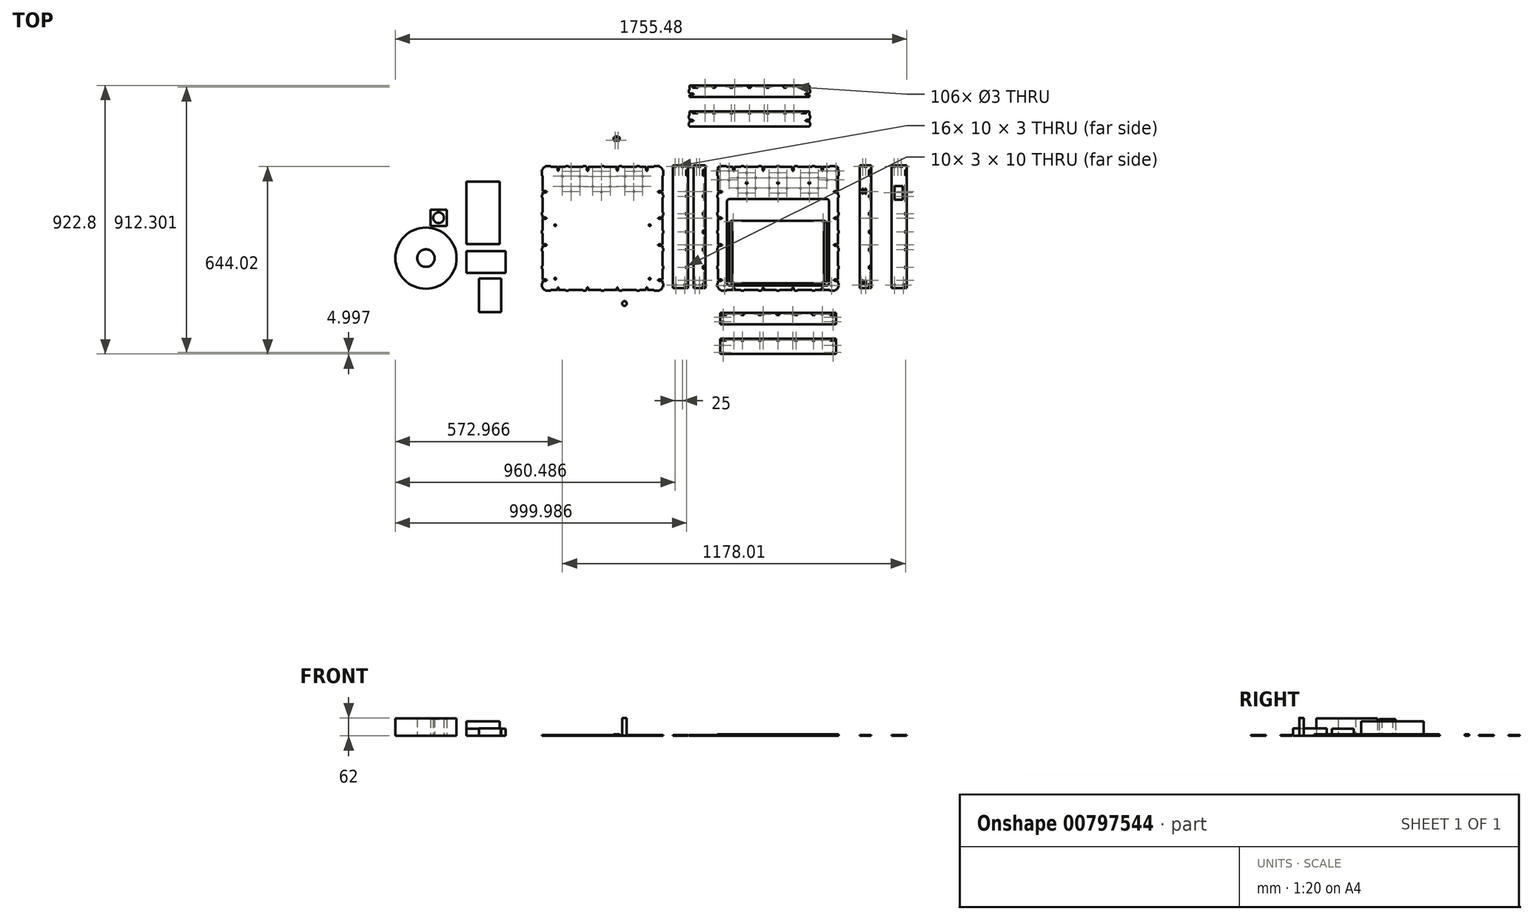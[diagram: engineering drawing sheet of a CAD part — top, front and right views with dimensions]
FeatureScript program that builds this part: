
annotation { "Feature Type Name" : "Feature", "Feature Type Description" : "" }
export const myFeature = defineFeature(function(context is Context, id is Id, definition is map)
    precondition{}
    {
        {
            var Q0;
            Q0=qCreatedBy(makeId("Top.planeOp"),FACE);
            var sketch = newSketch(context, id + "F0", { "sketchPlane" : qUnion([Q0])});
            skCircle(sketch, "E0", {"center": v(-429.2, -257.83) * mm, "radius": 8 * mm});
            skSolve(sketch);
        }
        {
            var Q0;
            Q0=makeQuery(id+"F0.imprint","IMPRINT",FACE,{"disambiguationData":[TD([[makeQuery(id+"F0.imprint","IMPRINT",EDGE,{"derivedFrom":sQuery(id+"F0.wireOp",EDGE,"E0")}),1.0]])]});
            extrude(context, id + "F1", {"entities" : qUnion([Q0]), "depth" : 62 * mm, "offsetDistance" : 25 * mm});
        }
        {
            var Q0;
            Q0=qCreatedBy(makeId("Top.planeOp"),FACE);
            var sketch = newSketch(context, id + "F2", { "sketchPlane" : qUnion([Q0])});
            skLineSegment(sketch, "E1", {"start": v(147.3, -211.25) * mm, "end": v(103, -211.25) * mm});
            skLineSegment(sketch, "E2", {"start": v(147.3, -208.35) * mm, "end": v(147.3, -211.25) * mm});
            skLineSegment(sketch, "E3", {"start": v(147.3, -208.35) * mm, "end": v(145.8, -208.35) * mm});
            skLineSegment(sketch, "E4", {"start": v(145.8, -205.75) * mm, "end": v(145.8, -208.35) * mm});
            skLineSegment(sketch, "E5", {"start": v(147.3, -205.75) * mm, "end": v(145.8, -205.75) * mm});
            skLineSegment(sketch, "E6", {"start": v(147.3, -202.75) * mm, "end": v(147.3, -205.75) * mm});
            skLineSegment(sketch, "E7", {"start": v(150.7, -202.75) * mm, "end": v(147.3, -202.75) * mm});
            skLineSegment(sketch, "E8", {"start": v(150.7, -205.75) * mm, "end": v(150.7, -202.75) * mm});
            skLineSegment(sketch, "E9", {"start": v(152.2, -205.75) * mm, "end": v(150.7, -205.75) * mm});
            skLineSegment(sketch, "E10", {"start": v(152.2, -208.35) * mm, "end": v(152.2, -205.75) * mm});
            skLineSegment(sketch, "E11", {"start": v(152.2, -208.35) * mm, "end": v(150.7, -208.35) * mm});
            skLineSegment(sketch, "E12", {"start": v(150.7, -211.25) * mm, "end": v(150.7, -208.35) * mm});
            skLineSegment(sketch, "E13", {"start": v(155, -211.25) * mm, "end": v(150.7, -211.25) * mm});
            skLineSegment(sketch, "E14", {"start": v(155, -214.25) * mm, "end": v(155, -211.25) * mm});
            skLineSegment(sketch, "E15", {"start": v(165, -214.25) * mm, "end": v(155, -214.25) * mm});
            skLineSegment(sketch, "E16", {"start": v(165, -211.25) * mm, "end": v(165, -214.25) * mm});
            skLineSegment(sketch, "E17", {"start": v(215, -211.25) * mm, "end": v(165, -211.25) * mm});
            skLineSegment(sketch, "E18", {"start": v(215, -214.25) * mm, "end": v(215, -211.25) * mm});
            skLineSegment(sketch, "E19", {"start": v(225, -214.25) * mm, "end": v(215, -214.25) * mm});
            skLineSegment(sketch, "E20", {"start": v(225, -211.25) * mm, "end": v(225, -214.25) * mm});
            skLineSegment(sketch, "E21", {"start": v(248.3, -211.25) * mm, "end": v(225, -211.25) * mm});
            skLineSegment(sketch, "E22", {"start": v(248.3, -208.35) * mm, "end": v(248.3, -211.25) * mm});
            skLineSegment(sketch, "E23", {"start": v(246.8, -208.35) * mm, "end": v(248.3, -208.35) * mm});
            skLineSegment(sketch, "E24", {"start": v(246.8, -205.75) * mm, "end": v(246.8, -208.35) * mm});
            skLineSegment(sketch, "E25", {"start": v(248.3, -205.75) * mm, "end": v(246.8, -205.75) * mm});
            skLineSegment(sketch, "E26", {"start": v(248.3, -202.75) * mm, "end": v(248.3, -205.75) * mm});
            skLineSegment(sketch, "E27", {"start": v(251.7, -202.75) * mm, "end": v(248.3, -202.75) * mm});
            skLineSegment(sketch, "E28", {"start": v(251.7, -205.75) * mm, "end": v(251.7, -202.75) * mm});
            skLineSegment(sketch, "E29", {"start": v(253.2, -205.75) * mm, "end": v(251.7, -205.75) * mm});
            skLineSegment(sketch, "E30", {"start": v(253.2, -208.35) * mm, "end": v(253.2, -205.75) * mm});
            skLineSegment(sketch, "E31", {"start": v(251.7, -208.35) * mm, "end": v(253.2, -208.35) * mm});
            skLineSegment(sketch, "E32", {"start": v(251.7, -211.25) * mm, "end": v(251.7, -208.35) * mm});
            skLineSegment(sketch, "E33", {"start": v(275, -211.25) * mm, "end": v(251.7, -211.25) * mm});
            skLineSegment(sketch, "E34", {"start": v(275, -214.25) * mm, "end": v(275, -211.25) * mm});
            skLineSegment(sketch, "E35", {"start": v(293.5, -214.25) * mm, "end": v(275, -214.25) * mm});
            skLineSegment(sketch, "E36", {"start": v(293.5, -211.25) * mm, "end": v(293.5, -214.25) * mm});
            skArc(sketch, "E37", {"start": v(303.5, -201.25) * mm, "mid": v(300.57, -208.32) * mm, "end": v(293.5, -211.25) * mm});
            skLineSegment(sketch, "E38", {"start": v(306.5, -201.25) * mm, "end": v(303.5, -201.25) * mm});
            skLineSegment(sketch, "E39", {"start": v(306.5, -188.25) * mm, "end": v(306.5, -201.25) * mm});
            skLineSegment(sketch, "E40", {"start": v(303.5, -188.25) * mm, "end": v(306.5, -188.25) * mm});
            skLineSegment(sketch, "E41", {"start": v(303.5, -179.45) * mm, "end": v(303.5, -188.25) * mm});
            skLineSegment(sketch, "E42", {"start": v(297.1, -179.45) * mm, "end": v(303.5, -179.45) * mm});
            skLineSegment(sketch, "E43", {"start": v(297.1, -180.95) * mm, "end": v(297.1, -179.45) * mm});
            skLineSegment(sketch, "E44", {"start": v(294.5, -180.95) * mm, "end": v(297.1, -180.95) * mm});
            skLineSegment(sketch, "E45", {"start": v(294.5, -179.45) * mm, "end": v(294.5, -180.95) * mm});
            skLineSegment(sketch, "E46", {"start": v(289.5, -179.45) * mm, "end": v(294.5, -179.45) * mm});
            skLineSegment(sketch, "E47", {"start": v(289.5, -176.05) * mm, "end": v(289.5, -179.45) * mm});
            skLineSegment(sketch, "E48", {"start": v(294.5, -176.05) * mm, "end": v(289.5, -176.05) * mm});
            skLineSegment(sketch, "E49", {"start": v(294.5, -174.55) * mm, "end": v(294.5, -176.05) * mm});
            skLineSegment(sketch, "E50", {"start": v(297.1, -174.55) * mm, "end": v(294.5, -174.55) * mm});
            skLineSegment(sketch, "E51", {"start": v(297.1, -176.05) * mm, "end": v(297.1, -174.55) * mm});
            skLineSegment(sketch, "E52", {"start": v(303.5, -176.05) * mm, "end": v(297.1, -176.05) * mm});
            skLineSegment(sketch, "E53", {"start": v(303.5, -138.25) * mm, "end": v(303.5, -176.05) * mm});
            skLineSegment(sketch, "E54", {"start": v(306.5, -138.25) * mm, "end": v(303.5, -138.25) * mm});
            skLineSegment(sketch, "E55", {"start": v(306.5, -128.25) * mm, "end": v(306.5, -138.25) * mm});
            skLineSegment(sketch, "E56", {"start": v(303.5, -128.25) * mm, "end": v(306.5, -128.25) * mm});
            skLineSegment(sketch, "E57", {"start": v(303.5, -78.25) * mm, "end": v(303.5, -128.25) * mm});
            skLineSegment(sketch, "E58", {"start": v(306.5, -78.25) * mm, "end": v(303.5, -78.25) * mm});
            skLineSegment(sketch, "E59", {"start": v(306.5, -68.25) * mm, "end": v(306.5, -78.25) * mm});
            skLineSegment(sketch, "E60", {"start": v(303.5, -68.25) * mm, "end": v(306.5, -68.25) * mm});
            skLineSegment(sketch, "E61", {"start": v(303.5, -58.45) * mm, "end": v(303.5, -68.25) * mm});
            skLineSegment(sketch, "E62", {"start": v(297.1, -58.45) * mm, "end": v(303.5, -58.45) * mm});
            skLineSegment(sketch, "E63", {"start": v(297.1, -59.95) * mm, "end": v(297.1, -58.45) * mm});
            skLineSegment(sketch, "E64", {"start": v(294.5, -59.95) * mm, "end": v(297.1, -59.95) * mm});
            skLineSegment(sketch, "E65", {"start": v(294.5, -58.45) * mm, "end": v(294.5, -59.95) * mm});
            skLineSegment(sketch, "E66", {"start": v(289.5, -58.45) * mm, "end": v(294.5, -58.45) * mm});
            skLineSegment(sketch, "E67", {"start": v(289.5, -55.05) * mm, "end": v(289.5, -58.45) * mm});
            skLineSegment(sketch, "E68", {"start": v(294.5, -55.05) * mm, "end": v(289.5, -55.05) * mm});
            skLineSegment(sketch, "E69", {"start": v(294.5, -53.55) * mm, "end": v(294.5, -55.05) * mm});
            skLineSegment(sketch, "E70", {"start": v(297.1, -53.55) * mm, "end": v(294.5, -53.55) * mm});
            skLineSegment(sketch, "E71", {"start": v(297.1, -55.05) * mm, "end": v(297.1, -53.55) * mm});
            skLineSegment(sketch, "E72", {"start": v(303.5, -55.05) * mm, "end": v(297.1, -55.05) * mm});
            skLineSegment(sketch, "E73", {"start": v(303.5, -16.25) * mm, "end": v(303.5, -55.05) * mm});
            skLineSegment(sketch, "E74", {"start": v(306.5, -16.25) * mm, "end": v(303.5, -16.25) * mm});
            skLineSegment(sketch, "E75", {"start": v(306.5, -6.25) * mm, "end": v(306.5, -16.25) * mm});
            skLineSegment(sketch, "E76", {"start": v(303.5, -6.25) * mm, "end": v(306.5, -6.25) * mm});
            skLineSegment(sketch, "E77", {"start": v(303.5, 33.55) * mm, "end": v(303.5, -6.25) * mm});
            skLineSegment(sketch, "E78", {"start": v(297.1, 33.55) * mm, "end": v(303.5, 33.55) * mm});
            skLineSegment(sketch, "E79", {"start": v(297.1, 33.55) * mm, "end": v(297.1, 32.05) * mm});
            skLineSegment(sketch, "E80", {"start": v(294.5, 32.05) * mm, "end": v(297.1, 32.05) * mm});
            skLineSegment(sketch, "E81", {"start": v(294.5, 33.55) * mm, "end": v(294.5, 32.05) * mm});
            skLineSegment(sketch, "E82", {"start": v(289.5, 33.55) * mm, "end": v(294.5, 33.55) * mm});
            skLineSegment(sketch, "E83", {"start": v(289.5, 36.95) * mm, "end": v(289.5, 33.55) * mm});
            skLineSegment(sketch, "E84", {"start": v(294.5, 36.95) * mm, "end": v(289.5, 36.95) * mm});
            skLineSegment(sketch, "E85", {"start": v(294.5, 38.45) * mm, "end": v(294.5, 36.95) * mm});
            skLineSegment(sketch, "E86", {"start": v(297.1, 38.45) * mm, "end": v(294.5, 38.45) * mm});
            skLineSegment(sketch, "E87", {"start": v(297.1, 38.45) * mm, "end": v(297.1, 36.95) * mm});
            skLineSegment(sketch, "E88", {"start": v(303.5, 36.95) * mm, "end": v(297.1, 36.95) * mm});
            skLineSegment(sketch, "E89", {"start": v(303.5, 45.75) * mm, "end": v(303.5, 36.95) * mm});
            skLineSegment(sketch, "E90", {"start": v(306.5, 45.75) * mm, "end": v(303.5, 45.75) * mm});
            skLineSegment(sketch, "E91", {"start": v(306.5, 55.75) * mm, "end": v(306.5, 45.75) * mm});
            skLineSegment(sketch, "E92", {"start": v(303.5, 55.75) * mm, "end": v(306.5, 55.75) * mm});
            skLineSegment(sketch, "E93", {"start": v(303.5, 105.75) * mm, "end": v(303.5, 55.75) * mm});
            skLineSegment(sketch, "E94", {"start": v(306.5, 105.75) * mm, "end": v(303.5, 105.75) * mm});
            skLineSegment(sketch, "E95", {"start": v(306.5, 115.75) * mm, "end": v(306.5, 105.75) * mm});
            skLineSegment(sketch, "E96", {"start": v(303.5, 115.75) * mm, "end": v(306.5, 115.75) * mm});
            skLineSegment(sketch, "E97", {"start": v(303.5, 124.55) * mm, "end": v(303.5, 115.75) * mm});
            skLineSegment(sketch, "E98", {"start": v(297.1, 124.55) * mm, "end": v(303.5, 124.55) * mm});
            skLineSegment(sketch, "E99", {"start": v(297.1, 123.05) * mm, "end": v(297.1, 124.55) * mm});
            skLineSegment(sketch, "E100", {"start": v(294.5, 123.05) * mm, "end": v(297.1, 123.05) * mm});
            skLineSegment(sketch, "E101", {"start": v(294.5, 124.55) * mm, "end": v(294.5, 123.05) * mm});
            skLineSegment(sketch, "E102", {"start": v(289.5, 124.55) * mm, "end": v(294.5, 124.55) * mm});
            skLineSegment(sketch, "E103", {"start": v(289.5, 127.95) * mm, "end": v(289.5, 124.55) * mm});
            skLineSegment(sketch, "E104", {"start": v(294.5, 127.95) * mm, "end": v(289.5, 127.95) * mm});
            skLineSegment(sketch, "E105", {"start": v(294.5, 129.45) * mm, "end": v(294.5, 127.95) * mm});
            skLineSegment(sketch, "E106", {"start": v(297.1, 129.45) * mm, "end": v(294.5, 129.45) * mm});
            skLineSegment(sketch, "E107", {"start": v(297.1, 127.95) * mm, "end": v(297.1, 129.45) * mm});
            skLineSegment(sketch, "E108", {"start": v(303.5, 127.95) * mm, "end": v(297.1, 127.95) * mm});
            skLineSegment(sketch, "E109", {"start": v(303.5, 181.25) * mm, "end": v(303.5, 127.95) * mm});
            skLineSegment(sketch, "E110", {"start": v(306.5, 181.25) * mm, "end": v(303.5, 181.25) * mm});
            skLineSegment(sketch, "E111", {"start": v(306.5, 201.25) * mm, "end": v(306.5, 181.25) * mm});
            skLineSegment(sketch, "E112", {"start": v(303.5, 201.25) * mm, "end": v(306.5, 201.25) * mm});
            skLineSegment(sketch, "E113", {"start": v(293.5, 214.25) * mm, "end": v(293.5, 211.25) * mm});
            skLineSegment(sketch, "E114", {"start": v(275, 214.25) * mm, "end": v(293.5, 214.25) * mm});
            skLineSegment(sketch, "E115", {"start": v(275, 211.25) * mm, "end": v(275, 214.25) * mm});
            skLineSegment(sketch, "E116", {"start": v(251.7, 211.25) * mm, "end": v(275, 211.25) * mm});
            skLineSegment(sketch, "E117", {"start": v(251.7, 204.85) * mm, "end": v(251.7, 211.25) * mm});
            skLineSegment(sketch, "E118", {"start": v(253.2, 204.85) * mm, "end": v(251.7, 204.85) * mm});
            skLineSegment(sketch, "E119", {"start": v(253.2, 202.25) * mm, "end": v(253.2, 204.85) * mm});
            skLineSegment(sketch, "E120", {"start": v(251.7, 202.25) * mm, "end": v(253.2, 202.25) * mm});
            skLineSegment(sketch, "E121", {"start": v(251.7, 197.25) * mm, "end": v(251.7, 202.25) * mm});
            skLineSegment(sketch, "E122", {"start": v(248.3, 197.25) * mm, "end": v(251.7, 197.25) * mm});
            skLineSegment(sketch, "E123", {"start": v(248.3, 202.25) * mm, "end": v(248.3, 197.25) * mm});
            skLineSegment(sketch, "E124", {"start": v(246.8, 202.25) * mm, "end": v(248.3, 202.25) * mm});
            skLineSegment(sketch, "E125", {"start": v(246.8, 204.85) * mm, "end": v(246.8, 202.25) * mm});
            skLineSegment(sketch, "E126", {"start": v(248.3, 204.85) * mm, "end": v(246.8, 204.85) * mm});
            skLineSegment(sketch, "E127", {"start": v(248.3, 211.25) * mm, "end": v(248.3, 204.85) * mm});
            skLineSegment(sketch, "E128", {"start": v(225, 211.25) * mm, "end": v(248.3, 211.25) * mm});
            skLineSegment(sketch, "E129", {"start": v(225, 214.25) * mm, "end": v(225, 211.25) * mm});
            skLineSegment(sketch, "E130", {"start": v(215, 214.25) * mm, "end": v(225, 214.25) * mm});
            skLineSegment(sketch, "E131", {"start": v(215, 211.25) * mm, "end": v(215, 214.25) * mm});
            skLineSegment(sketch, "E132", {"start": v(165, 211.25) * mm, "end": v(215, 211.25) * mm});
            skLineSegment(sketch, "E133", {"start": v(165, 214.25) * mm, "end": v(165, 211.25) * mm});
            skLineSegment(sketch, "E134", {"start": v(155, 214.25) * mm, "end": v(165, 214.25) * mm});
            skLineSegment(sketch, "E135", {"start": v(155, 211.25) * mm, "end": v(155, 214.25) * mm});
            skLineSegment(sketch, "E136", {"start": v(150.7, 211.25) * mm, "end": v(155, 211.25) * mm});
            skLineSegment(sketch, "E137", {"start": v(150.7, 204.85) * mm, "end": v(150.7, 211.25) * mm});
            skLineSegment(sketch, "E138", {"start": v(152.2, 204.85) * mm, "end": v(150.7, 204.85) * mm});
            skLineSegment(sketch, "E139", {"start": v(152.2, 202.25) * mm, "end": v(152.2, 204.85) * mm});
            skLineSegment(sketch, "E140", {"start": v(152.2, 202.25) * mm, "end": v(150.7, 202.25) * mm});
            skLineSegment(sketch, "E141", {"start": v(150.7, 197.25) * mm, "end": v(150.7, 202.25) * mm});
            skLineSegment(sketch, "E142", {"start": v(147.3, 197.25) * mm, "end": v(150.7, 197.25) * mm});
            skLineSegment(sketch, "E143", {"start": v(147.3, 202.25) * mm, "end": v(147.3, 197.25) * mm});
            skLineSegment(sketch, "E144", {"start": v(147.3, 202.25) * mm, "end": v(145.8, 202.25) * mm});
            skLineSegment(sketch, "E145", {"start": v(145.8, 204.85) * mm, "end": v(145.8, 202.25) * mm});
            skLineSegment(sketch, "E146", {"start": v(147.3, 204.85) * mm, "end": v(145.8, 204.85) * mm});
            skLineSegment(sketch, "E147", {"start": v(147.3, 211.25) * mm, "end": v(147.3, 204.85) * mm});
            skLineSegment(sketch, "E148", {"start": v(103, 211.25) * mm, "end": v(147.3, 211.25) * mm});
            skLineSegment(sketch, "E149", {"start": v(103, 214.25) * mm, "end": v(103, 211.25) * mm});
            skLineSegment(sketch, "E150", {"start": v(93, 214.25) * mm, "end": v(103, 214.25) * mm});
            skLineSegment(sketch, "E151", {"start": v(93, 211.25) * mm, "end": v(93, 214.25) * mm});
            skLineSegment(sketch, "E152", {"start": v(48.7, 211.25) * mm, "end": v(93, 211.25) * mm});
            skLineSegment(sketch, "E153", {"start": v(48.7, 204.85) * mm, "end": v(48.7, 211.25) * mm});
            skLineSegment(sketch, "E154", {"start": v(48.7, 204.85) * mm, "end": v(50.2, 204.85) * mm});
            skLineSegment(sketch, "E155", {"start": v(50.2, 202.25) * mm, "end": v(50.2, 204.85) * mm});
            skLineSegment(sketch, "E156", {"start": v(48.7, 202.25) * mm, "end": v(50.2, 202.25) * mm});
            skLineSegment(sketch, "E157", {"start": v(48.7, 197.25) * mm, "end": v(48.7, 202.25) * mm});
            skLineSegment(sketch, "E158", {"start": v(45.3, 197.25) * mm, "end": v(48.7, 197.25) * mm});
            skLineSegment(sketch, "E159", {"start": v(45.3, 202.25) * mm, "end": v(45.3, 197.25) * mm});
            skLineSegment(sketch, "E160", {"start": v(43.8, 202.25) * mm, "end": v(45.3, 202.25) * mm});
            skLineSegment(sketch, "E161", {"start": v(43.8, 204.85) * mm, "end": v(43.8, 202.25) * mm});
            skLineSegment(sketch, "E162", {"start": v(43.8, 204.85) * mm, "end": v(45.3, 204.85) * mm});
            skLineSegment(sketch, "E163", {"start": v(45.3, 211.25) * mm, "end": v(45.3, 204.85) * mm});
            skLineSegment(sketch, "E164", {"start": v(41, 211.25) * mm, "end": v(45.3, 211.25) * mm});
            skLineSegment(sketch, "E165", {"start": v(41, 214.25) * mm, "end": v(41, 211.25) * mm});
            skLineSegment(sketch, "E166", {"start": v(31, 214.25) * mm, "end": v(41, 214.25) * mm});
            skLineSegment(sketch, "E167", {"start": v(31, 211.25) * mm, "end": v(31, 214.25) * mm});
            skLineSegment(sketch, "E168", {"start": v(-19, 211.25) * mm, "end": v(31, 211.25) * mm});
            skLineSegment(sketch, "E169", {"start": v(-19, 214.25) * mm, "end": v(-19, 211.25) * mm});
            skLineSegment(sketch, "E170", {"start": v(-29, 214.25) * mm, "end": v(-19, 214.25) * mm});
            skLineSegment(sketch, "E171", {"start": v(-29, 211.25) * mm, "end": v(-29, 214.25) * mm});
            skLineSegment(sketch, "E172", {"start": v(-52.3, 211.25) * mm, "end": v(-29, 211.25) * mm});
            skLineSegment(sketch, "E173", {"start": v(-52.3, 204.85) * mm, "end": v(-52.3, 211.25) * mm});
            skLineSegment(sketch, "E174", {"start": v(-50.8, 204.85) * mm, "end": v(-52.3, 204.85) * mm});
            skLineSegment(sketch, "E175", {"start": v(-50.8, 202.25) * mm, "end": v(-50.8, 204.85) * mm});
            skLineSegment(sketch, "E176", {"start": v(-52.3, 202.25) * mm, "end": v(-50.8, 202.25) * mm});
            skLineSegment(sketch, "E177", {"start": v(-52.3, 197.25) * mm, "end": v(-52.3, 202.25) * mm});
            skLineSegment(sketch, "E178", {"start": v(-55.7, 197.25) * mm, "end": v(-52.3, 197.25) * mm});
            skLineSegment(sketch, "E179", {"start": v(-55.7, 202.25) * mm, "end": v(-55.7, 197.25) * mm});
            skLineSegment(sketch, "E180", {"start": v(-57.2, 202.25) * mm, "end": v(-55.7, 202.25) * mm});
            skLineSegment(sketch, "E181", {"start": v(-57.2, 204.85) * mm, "end": v(-57.2, 202.25) * mm});
            skLineSegment(sketch, "E182", {"start": v(-55.7, 204.85) * mm, "end": v(-57.2, 204.85) * mm});
            skLineSegment(sketch, "E183", {"start": v(-55.7, 211.25) * mm, "end": v(-55.7, 204.85) * mm});
            skLineSegment(sketch, "E184", {"start": v(-79, 211.25) * mm, "end": v(-55.7, 211.25) * mm});
            skLineSegment(sketch, "E185", {"start": v(-79, 214.25) * mm, "end": v(-79, 211.25) * mm});
            skLineSegment(sketch, "E186", {"start": v(-97.5, 214.25) * mm, "end": v(-79, 214.25) * mm});
            skLineSegment(sketch, "E187", {"start": v(-97.5, 211.25) * mm, "end": v(-97.5, 214.25) * mm});
            skLineSegment(sketch, "E188", {"start": v(-110.5, 201.25) * mm, "end": v(-107.5, 201.25) * mm});
            skLineSegment(sketch, "E189", {"start": v(-110.5, 181.25) * mm, "end": v(-110.5, 201.25) * mm});
            skLineSegment(sketch, "E190", {"start": v(-107.5, 181.25) * mm, "end": v(-110.5, 181.25) * mm});
            skLineSegment(sketch, "E191", {"start": v(-107.5, 127.95) * mm, "end": v(-107.5, 181.25) * mm});
            skLineSegment(sketch, "E192", {"start": v(-101.1, 127.95) * mm, "end": v(-107.5, 127.95) * mm});
            skLineSegment(sketch, "E193", {"start": v(-101.1, 129.45) * mm, "end": v(-101.1, 127.95) * mm});
            skLineSegment(sketch, "E194", {"start": v(-98.5, 129.45) * mm, "end": v(-101.1, 129.45) * mm});
            skLineSegment(sketch, "E195", {"start": v(-98.5, 127.95) * mm, "end": v(-98.5, 129.45) * mm});
            skLineSegment(sketch, "E196", {"start": v(-93.5, 127.95) * mm, "end": v(-98.5, 127.95) * mm});
            skLineSegment(sketch, "E197", {"start": v(-93.5, 124.55) * mm, "end": v(-93.5, 127.95) * mm});
            skLineSegment(sketch, "E198", {"start": v(-98.5, 124.55) * mm, "end": v(-93.5, 124.55) * mm});
            skLineSegment(sketch, "E199", {"start": v(-98.5, 123.05) * mm, "end": v(-98.5, 124.55) * mm});
            skLineSegment(sketch, "E200", {"start": v(-101.1, 123.05) * mm, "end": v(-98.5, 123.05) * mm});
            skLineSegment(sketch, "E201", {"start": v(-101.1, 124.55) * mm, "end": v(-101.1, 123.05) * mm});
            skLineSegment(sketch, "E202", {"start": v(-107.5, 124.55) * mm, "end": v(-101.1, 124.55) * mm});
            skLineSegment(sketch, "E203", {"start": v(-107.5, 115.75) * mm, "end": v(-107.5, 124.55) * mm});
            skLineSegment(sketch, "E204", {"start": v(-110.5, 115.75) * mm, "end": v(-107.5, 115.75) * mm});
            skLineSegment(sketch, "E205", {"start": v(-110.5, 105.75) * mm, "end": v(-110.5, 115.75) * mm});
            skLineSegment(sketch, "E206", {"start": v(-107.5, 105.75) * mm, "end": v(-110.5, 105.75) * mm});
            skLineSegment(sketch, "E207", {"start": v(-107.5, 55.75) * mm, "end": v(-107.5, 105.75) * mm});
            skLineSegment(sketch, "E208", {"start": v(-110.5, 55.75) * mm, "end": v(-107.5, 55.75) * mm});
            skLineSegment(sketch, "E209", {"start": v(-110.5, 45.75) * mm, "end": v(-110.5, 55.75) * mm});
            skLineSegment(sketch, "E210", {"start": v(-107.5, 45.75) * mm, "end": v(-110.5, 45.75) * mm});
            skLineSegment(sketch, "E211", {"start": v(-107.5, 36.95) * mm, "end": v(-107.5, 45.75) * mm});
            skLineSegment(sketch, "E212", {"start": v(-101.1, 36.95) * mm, "end": v(-107.5, 36.95) * mm});
            skLineSegment(sketch, "E213", {"start": v(-101.1, 38.45) * mm, "end": v(-101.1, 36.95) * mm});
            skLineSegment(sketch, "E214", {"start": v(-98.5, 38.45) * mm, "end": v(-101.1, 38.45) * mm});
            skLineSegment(sketch, "E215", {"start": v(-98.5, 38.45) * mm, "end": v(-98.5, 36.95) * mm});
            skLineSegment(sketch, "E216", {"start": v(-93.5, 36.95) * mm, "end": v(-98.5, 36.95) * mm});
            skLineSegment(sketch, "E217", {"start": v(-93.5, 33.55) * mm, "end": v(-93.5, 36.95) * mm});
            skLineSegment(sketch, "E218", {"start": v(-98.5, 33.55) * mm, "end": v(-93.5, 33.55) * mm});
            skLineSegment(sketch, "E219", {"start": v(-98.5, 33.55) * mm, "end": v(-98.5, 32.05) * mm});
            skLineSegment(sketch, "E220", {"start": v(-101.1, 32.05) * mm, "end": v(-98.5, 32.05) * mm});
            skLineSegment(sketch, "E221", {"start": v(-101.1, 33.55) * mm, "end": v(-101.1, 32.05) * mm});
            skLineSegment(sketch, "E222", {"start": v(-107.5, 33.55) * mm, "end": v(-101.1, 33.55) * mm});
            skLineSegment(sketch, "E223", {"start": v(-107.5, -6.25) * mm, "end": v(-107.5, 33.55) * mm});
            skLineSegment(sketch, "E224", {"start": v(-110.5, -6.25) * mm, "end": v(-107.5, -6.25) * mm});
            skLineSegment(sketch, "E225", {"start": v(-110.5, -16.25) * mm, "end": v(-110.5, -6.25) * mm});
            skLineSegment(sketch, "E226", {"start": v(-107.5, -16.25) * mm, "end": v(-110.5, -16.25) * mm});
            skLineSegment(sketch, "E227", {"start": v(-107.5, -55.05) * mm, "end": v(-107.5, -16.25) * mm});
            skLineSegment(sketch, "E228", {"start": v(-101.1, -55.05) * mm, "end": v(-107.5, -55.05) * mm});
            skLineSegment(sketch, "E229", {"start": v(-101.1, -53.55) * mm, "end": v(-101.1, -55.05) * mm});
            skLineSegment(sketch, "E230", {"start": v(-98.5, -53.55) * mm, "end": v(-101.1, -53.55) * mm});
            skLineSegment(sketch, "E231", {"start": v(-98.5, -55.05) * mm, "end": v(-98.5, -53.55) * mm});
            skLineSegment(sketch, "E232", {"start": v(-93.5, -55.05) * mm, "end": v(-98.5, -55.05) * mm});
            skLineSegment(sketch, "E233", {"start": v(-93.5, -58.45) * mm, "end": v(-93.5, -55.05) * mm});
            skLineSegment(sketch, "E234", {"start": v(-98.5, -58.45) * mm, "end": v(-93.5, -58.45) * mm});
            skLineSegment(sketch, "E235", {"start": v(-98.5, -59.95) * mm, "end": v(-98.5, -58.45) * mm});
            skLineSegment(sketch, "E236", {"start": v(-101.1, -59.95) * mm, "end": v(-98.5, -59.95) * mm});
            skLineSegment(sketch, "E237", {"start": v(-101.1, -58.45) * mm, "end": v(-101.1, -59.95) * mm});
            skLineSegment(sketch, "E238", {"start": v(-107.5, -58.45) * mm, "end": v(-101.1, -58.45) * mm});
            skLineSegment(sketch, "E239", {"start": v(-107.5, -68.25) * mm, "end": v(-107.5, -58.45) * mm});
            skLineSegment(sketch, "E240", {"start": v(-110.5, -68.25) * mm, "end": v(-107.5, -68.25) * mm});
            skLineSegment(sketch, "E241", {"start": v(-110.5, -78.25) * mm, "end": v(-110.5, -68.25) * mm});
            skLineSegment(sketch, "E242", {"start": v(-107.5, -78.25) * mm, "end": v(-110.5, -78.25) * mm});
            skLineSegment(sketch, "E243", {"start": v(-107.5, -128.25) * mm, "end": v(-107.5, -78.25) * mm});
            skLineSegment(sketch, "E244", {"start": v(-110.5, -128.25) * mm, "end": v(-107.5, -128.25) * mm});
            skLineSegment(sketch, "E245", {"start": v(-110.5, -138.25) * mm, "end": v(-110.5, -128.25) * mm});
            skLineSegment(sketch, "E246", {"start": v(-107.5, -138.25) * mm, "end": v(-110.5, -138.25) * mm});
            skLineSegment(sketch, "E247", {"start": v(-107.5, -176.05) * mm, "end": v(-107.5, -138.25) * mm});
            skLineSegment(sketch, "E248", {"start": v(-101.1, -176.05) * mm, "end": v(-107.5, -176.05) * mm});
            skLineSegment(sketch, "E249", {"start": v(-101.1, -174.55) * mm, "end": v(-101.1, -176.05) * mm});
            skLineSegment(sketch, "E250", {"start": v(-98.5, -174.55) * mm, "end": v(-101.1, -174.55) * mm});
            skLineSegment(sketch, "E251", {"start": v(-98.5, -176.05) * mm, "end": v(-98.5, -174.55) * mm});
            skLineSegment(sketch, "E252", {"start": v(-93.5, -176.05) * mm, "end": v(-98.5, -176.05) * mm});
            skLineSegment(sketch, "E253", {"start": v(-93.5, -179.45) * mm, "end": v(-93.5, -176.05) * mm});
            skLineSegment(sketch, "E254", {"start": v(-98.5, -179.45) * mm, "end": v(-93.5, -179.45) * mm});
            skLineSegment(sketch, "E255", {"start": v(-98.5, -180.95) * mm, "end": v(-98.5, -179.45) * mm});
            skLineSegment(sketch, "E256", {"start": v(-101.1, -180.95) * mm, "end": v(-98.5, -180.95) * mm});
            skLineSegment(sketch, "E257", {"start": v(-101.1, -179.45) * mm, "end": v(-101.1, -180.95) * mm});
            skLineSegment(sketch, "E258", {"start": v(-107.5, -179.45) * mm, "end": v(-101.1, -179.45) * mm});
            skLineSegment(sketch, "E259", {"start": v(-107.5, -188.25) * mm, "end": v(-107.5, -179.45) * mm});
            skLineSegment(sketch, "E260", {"start": v(-110.5, -188.25) * mm, "end": v(-107.5, -188.25) * mm});
            skLineSegment(sketch, "E261", {"start": v(-110.5, -201.25) * mm, "end": v(-110.5, -188.25) * mm});
            skLineSegment(sketch, "E262", {"start": v(-107.5, -201.25) * mm, "end": v(-110.5, -201.25) * mm});
            skArc(sketch, "E263", {"start": v(-107.5, -201.25) * mm, "mid": v(-104.57, -208.32) * mm, "end": v(-97.5, -211.25) * mm});
            skLineSegment(sketch, "E264", {"start": v(-97.5, -214.25) * mm, "end": v(-97.5, -211.25) * mm});
            skLineSegment(sketch, "E265", {"start": v(-79, -214.25) * mm, "end": v(-97.5, -214.25) * mm});
            skLineSegment(sketch, "E266", {"start": v(-79, -211.25) * mm, "end": v(-79, -214.25) * mm});
            skLineSegment(sketch, "E267", {"start": v(-55.7, -211.25) * mm, "end": v(-79, -211.25) * mm});
            skLineSegment(sketch, "E268", {"start": v(-55.7, -208.35) * mm, "end": v(-55.7, -211.25) * mm});
            skLineSegment(sketch, "E269", {"start": v(-57.2, -208.35) * mm, "end": v(-55.7, -208.35) * mm});
            skLineSegment(sketch, "E270", {"start": v(-57.2, -205.75) * mm, "end": v(-57.2, -208.35) * mm});
            skLineSegment(sketch, "E271", {"start": v(-55.7, -205.75) * mm, "end": v(-57.2, -205.75) * mm});
            skLineSegment(sketch, "E272", {"start": v(-55.7, -202.75) * mm, "end": v(-55.7, -205.75) * mm});
            skLineSegment(sketch, "E273", {"start": v(-52.3, -202.75) * mm, "end": v(-55.7, -202.75) * mm});
            skLineSegment(sketch, "E274", {"start": v(-52.3, -205.75) * mm, "end": v(-52.3, -202.75) * mm});
            skLineSegment(sketch, "E275", {"start": v(-50.8, -205.75) * mm, "end": v(-52.3, -205.75) * mm});
            skLineSegment(sketch, "E276", {"start": v(-50.8, -208.35) * mm, "end": v(-50.8, -205.75) * mm});
            skLineSegment(sketch, "E277", {"start": v(-52.3, -208.35) * mm, "end": v(-50.8, -208.35) * mm});
            skLineSegment(sketch, "E278", {"start": v(-52.3, -211.25) * mm, "end": v(-52.3, -208.35) * mm});
            skLineSegment(sketch, "E279", {"start": v(-29, -211.25) * mm, "end": v(-52.3, -211.25) * mm});
            skLineSegment(sketch, "E280", {"start": v(-29, -214.25) * mm, "end": v(-29, -211.25) * mm});
            skLineSegment(sketch, "E281", {"start": v(-19, -214.25) * mm, "end": v(-29, -214.25) * mm});
            skLineSegment(sketch, "E282", {"start": v(-19, -211.25) * mm, "end": v(-19, -214.25) * mm});
            skLineSegment(sketch, "E283", {"start": v(31, -211.25) * mm, "end": v(-19, -211.25) * mm});
            skLineSegment(sketch, "E284", {"start": v(31, -214.25) * mm, "end": v(31, -211.25) * mm});
            skLineSegment(sketch, "E285", {"start": v(41, -214.25) * mm, "end": v(31, -214.25) * mm});
            skLineSegment(sketch, "E286", {"start": v(41, -211.25) * mm, "end": v(41, -214.25) * mm});
            skLineSegment(sketch, "E287", {"start": v(45.3, -211.25) * mm, "end": v(41, -211.25) * mm});
            skLineSegment(sketch, "E288", {"start": v(45.3, -208.35) * mm, "end": v(45.3, -211.25) * mm});
            skLineSegment(sketch, "E289", {"start": v(43.8, -208.35) * mm, "end": v(45.3, -208.35) * mm});
            skLineSegment(sketch, "E290", {"start": v(43.8, -205.75) * mm, "end": v(43.8, -208.35) * mm});
            skLineSegment(sketch, "E291", {"start": v(43.8, -205.75) * mm, "end": v(45.3, -205.75) * mm});
            skLineSegment(sketch, "E292", {"start": v(45.3, -202.75) * mm, "end": v(45.3, -205.75) * mm});
            skLineSegment(sketch, "E293", {"start": v(48.7, -202.75) * mm, "end": v(45.3, -202.75) * mm});
            skLineSegment(sketch, "E294", {"start": v(48.7, -205.75) * mm, "end": v(48.7, -202.75) * mm});
            skLineSegment(sketch, "E295", {"start": v(48.7, -205.75) * mm, "end": v(50.2, -205.75) * mm});
            skLineSegment(sketch, "E296", {"start": v(50.2, -208.35) * mm, "end": v(50.2, -205.75) * mm});
            skLineSegment(sketch, "E297", {"start": v(48.7, -208.35) * mm, "end": v(50.2, -208.35) * mm});
            skLineSegment(sketch, "E298", {"start": v(48.7, -211.25) * mm, "end": v(48.7, -208.35) * mm});
            skLineSegment(sketch, "E299", {"start": v(93, -211.25) * mm, "end": v(48.7, -211.25) * mm});
            skLineSegment(sketch, "E300", {"start": v(93, -214.25) * mm, "end": v(93, -211.25) * mm});
            skLineSegment(sketch, "E301", {"start": v(103, -214.25) * mm, "end": v(93, -214.25) * mm});
            skLineSegment(sketch, "E302", {"start": v(103, -211.25) * mm, "end": v(103, -214.25) * mm});
            skCircle(sketch, "E303", {"center": v(-70, 166.75) * mm, "radius": 1.5 * mm});
            skCircle(sketch, "E304", {"center": v(-101, 166.75) * mm, "radius": 1.5 * mm});
            skCircle(sketch, "E305", {"center": v(-70, 197.75) * mm, "radius": 1.5 * mm});
            skCircle(sketch, "E306", {"center": v(-101, 197.75) * mm, "radius": 1.5 * mm});
            skCircle(sketch, "E307", {"center": v(266, 166.75) * mm, "radius": 1.5 * mm});
            skCircle(sketch, "E308", {"center": v(297, 166.75) * mm, "radius": 1.5 * mm});
            skCircle(sketch, "E309", {"center": v(297, 197.75) * mm, "radius": 1.5 * mm});
            skCircle(sketch, "E310", {"center": v(266, 197.75) * mm, "radius": 1.5 * mm});
            skCircle(sketch, "E311", {"center": v(281.5, -196.25) * mm, "radius": 1.5 * mm});
            skCircle(sketch, "E312", {"center": v(-85.5, -196.25) * mm, "radius": 1.5 * mm});
            skArc(sketch, "E313", {"start": v(263.5, -196.25) * mm, "mid": v(270.57, -193.32) * mm, "end": v(273.5, -186.25) * mm});
            skLineSegment(sketch, "E314", {"start": v(-67.5, -196.25) * mm, "end": v(263.5, -196.25) * mm});
            skArc(sketch, "E315", {"start": v(-67.5, -196.25) * mm, "mid": v(-74.57, -193.32) * mm, "end": v(-77.5, -186.25) * mm});
            skLineSegment(sketch, "E316", {"start": v(-77.5, 91.25) * mm, "end": v(-77.5, -186.25) * mm});
            skArc(sketch, "E317", {"start": v(-67.5, 101.25) * mm, "mid": v(-74.57, 98.32) * mm, "end": v(-77.5, 91.25) * mm});
            skLineSegment(sketch, "E318", {"start": v(263.5, 101.25) * mm, "end": v(-67.5, 101.25) * mm});
            skArc(sketch, "E319", {"start": v(263.5, 101.25) * mm, "mid": v(270.57, 98.32) * mm, "end": v(273.5, 91.25) * mm});
            skLineSegment(sketch, "E320", {"start": v(273.5, -186.25) * mm, "end": v(273.5, 91.25) * mm});
            skArc(sketch, "E321", {"start": v(-69, 16.25) * mm, "mid": v(-66.07, 23.32) * mm, "end": v(-59, 26.25) * mm});
            skArc(sketch, "E322", {"start": v(255, 26.25) * mm, "mid": v(262.07, 23.32) * mm, "end": v(265, 16.25) * mm});
            skArc(sketch, "E323", {"start": v(255, -187.75) * mm, "mid": v(262.07, -184.82) * mm, "end": v(265, -177.75) * mm});
            skArc(sketch, "E324", {"start": v(-59, -187.75) * mm, "mid": v(-66.07, -184.82) * mm, "end": v(-69, -177.75) * mm});
            skLineSegment(sketch, "E325", {"start": v(-59, 26.25) * mm, "end": v(255, 26.25) * mm});
            skCircle(sketch, "E326", {"center": v(-64, -172.75) * mm, "radius": 3 * mm});
            skCircle(sketch, "E327", {"center": v(-64, 11.25) * mm, "radius": 3 * mm});
            skCircle(sketch, "E328", {"center": v(260, 11.25) * mm, "radius": 3 * mm});
            skCircle(sketch, "E329", {"center": v(260, -172.75) * mm, "radius": 3 * mm});
            skLineSegment(sketch, "E330", {"start": v(-69, 16.25) * mm, "end": v(-69, -177.75) * mm});
            skLineSegment(sketch, "E331", {"start": v(265, 16.25) * mm, "end": v(265, -177.75) * mm});
            skCircle(sketch, "E332", {"center": v(-56.5, 23.75) * mm, "radius": 1.5 * mm});
            skCircle(sketch, "E333", {"center": v(252.5, 23.75) * mm, "radius": 1.5 * mm});
            skCircle(sketch, "E334", {"center": v(252.5, -185.25) * mm, "radius": 1.5 * mm});
            skCircle(sketch, "E335", {"center": v(-56.5, -185.25) * mm, "radius": 1.5 * mm});
            skLineSegment(sketch, "E336", {"start": v(-59, -187.75) * mm, "end": v(255, -187.75) * mm});
            skLineSegment(sketch, "E337", {"start": v(-59, -187.75) * mm, "end": v(-59, 26.25) * mm});
            skLineSegment(sketch, "E338", {"start": v(255, 26.25) * mm, "end": v(255, -187.75) * mm});
            skLineSegment(sketch, "E339", {"start": v(-455.3, -211.25) * mm, "end": v(-499.6, -211.25) * mm});
            skLineSegment(sketch, "E340", {"start": v(-455.3, -208.35) * mm, "end": v(-455.3, -211.25) * mm});
            skLineSegment(sketch, "E341", {"start": v(-455.3, -208.35) * mm, "end": v(-456.8, -208.35) * mm});
            skLineSegment(sketch, "E342", {"start": v(-456.8, -205.75) * mm, "end": v(-456.8, -208.35) * mm});
            skLineSegment(sketch, "E343", {"start": v(-455.3, -205.75) * mm, "end": v(-456.8, -205.75) * mm});
            skLineSegment(sketch, "E344", {"start": v(-455.3, -202.75) * mm, "end": v(-455.3, -205.75) * mm});
            skLineSegment(sketch, "E345", {"start": v(-451.9, -202.75) * mm, "end": v(-455.3, -202.75) * mm});
            skLineSegment(sketch, "E346", {"start": v(-451.9, -205.75) * mm, "end": v(-451.9, -202.75) * mm});
            skLineSegment(sketch, "E347", {"start": v(-450.4, -205.75) * mm, "end": v(-451.9, -205.75) * mm});
            skLineSegment(sketch, "E348", {"start": v(-450.4, -208.35) * mm, "end": v(-450.4, -205.75) * mm});
            skLineSegment(sketch, "E349", {"start": v(-450.4, -208.35) * mm, "end": v(-451.9, -208.35) * mm});
            skLineSegment(sketch, "E350", {"start": v(-451.9, -211.25) * mm, "end": v(-451.9, -208.35) * mm});
            skLineSegment(sketch, "E351", {"start": v(-447.6, -211.25) * mm, "end": v(-451.9, -211.25) * mm});
            skLineSegment(sketch, "E352", {"start": v(-447.6, -214.25) * mm, "end": v(-447.6, -211.25) * mm});
            skLineSegment(sketch, "E353", {"start": v(-437.6, -214.25) * mm, "end": v(-447.6, -214.25) * mm});
            skLineSegment(sketch, "E354", {"start": v(-437.6, -211.25) * mm, "end": v(-437.6, -214.25) * mm});
            skLineSegment(sketch, "E355", {"start": v(-387.6, -211.25) * mm, "end": v(-437.6, -211.25) * mm});
            skLineSegment(sketch, "E356", {"start": v(-387.6, -214.25) * mm, "end": v(-387.6, -211.25) * mm});
            skLineSegment(sketch, "E357", {"start": v(-377.6, -214.25) * mm, "end": v(-387.6, -214.25) * mm});
            skLineSegment(sketch, "E358", {"start": v(-377.6, -211.25) * mm, "end": v(-377.6, -214.25) * mm});
            skLineSegment(sketch, "E359", {"start": v(-354.3, -211.25) * mm, "end": v(-377.6, -211.25) * mm});
            skLineSegment(sketch, "E360", {"start": v(-354.3, -208.35) * mm, "end": v(-354.3, -211.25) * mm});
            skLineSegment(sketch, "E361", {"start": v(-355.8, -208.35) * mm, "end": v(-354.3, -208.35) * mm});
            skLineSegment(sketch, "E362", {"start": v(-355.8, -205.75) * mm, "end": v(-355.8, -208.35) * mm});
            skLineSegment(sketch, "E363", {"start": v(-354.3, -205.75) * mm, "end": v(-355.8, -205.75) * mm});
            skLineSegment(sketch, "E364", {"start": v(-354.3, -202.75) * mm, "end": v(-354.3, -205.75) * mm});
            skLineSegment(sketch, "E365", {"start": v(-350.9, -202.75) * mm, "end": v(-354.3, -202.75) * mm});
            skLineSegment(sketch, "E366", {"start": v(-350.9, -205.75) * mm, "end": v(-350.9, -202.75) * mm});
            skLineSegment(sketch, "E367", {"start": v(-349.4, -205.75) * mm, "end": v(-350.9, -205.75) * mm});
            skLineSegment(sketch, "E368", {"start": v(-349.4, -208.35) * mm, "end": v(-349.4, -205.75) * mm});
            skLineSegment(sketch, "E369", {"start": v(-350.9, -208.35) * mm, "end": v(-349.4, -208.35) * mm});
            skLineSegment(sketch, "E370", {"start": v(-350.9, -211.25) * mm, "end": v(-350.9, -208.35) * mm});
            skLineSegment(sketch, "E371", {"start": v(-327.6, -211.25) * mm, "end": v(-350.9, -211.25) * mm});
            skLineSegment(sketch, "E372", {"start": v(-327.6, -214.25) * mm, "end": v(-327.6, -211.25) * mm});
            skLineSegment(sketch, "E373", {"start": v(-309.1, -214.25) * mm, "end": v(-327.6, -214.25) * mm});
            skLineSegment(sketch, "E374", {"start": v(-309.1, -211.25) * mm, "end": v(-309.1, -214.25) * mm});
            skArc(sketch, "E375", {"start": v(-299.1, -201.25) * mm, "mid": v(-302.03, -208.32) * mm, "end": v(-309.1, -211.25) * mm});
            skLineSegment(sketch, "E376", {"start": v(-296.1, -201.25) * mm, "end": v(-299.1, -201.25) * mm});
            skLineSegment(sketch, "E377", {"start": v(-296.1, -188.25) * mm, "end": v(-296.1, -201.25) * mm});
            skLineSegment(sketch, "E378", {"start": v(-299.1, -188.25) * mm, "end": v(-296.1, -188.25) * mm});
            skLineSegment(sketch, "E379", {"start": v(-299.1, -179.45) * mm, "end": v(-299.1, -188.25) * mm});
            skLineSegment(sketch, "E380", {"start": v(-305.5, -179.45) * mm, "end": v(-299.1, -179.45) * mm});
            skLineSegment(sketch, "E381", {"start": v(-305.5, -180.95) * mm, "end": v(-305.5, -179.45) * mm});
            skLineSegment(sketch, "E382", {"start": v(-308.1, -180.95) * mm, "end": v(-305.5, -180.95) * mm});
            skLineSegment(sketch, "E383", {"start": v(-308.1, -179.45) * mm, "end": v(-308.1, -180.95) * mm});
            skLineSegment(sketch, "E384", {"start": v(-313.1, -179.45) * mm, "end": v(-308.1, -179.45) * mm});
            skLineSegment(sketch, "E385", {"start": v(-313.1, -176.05) * mm, "end": v(-313.1, -179.45) * mm});
            skLineSegment(sketch, "E386", {"start": v(-308.1, -176.05) * mm, "end": v(-313.1, -176.05) * mm});
            skLineSegment(sketch, "E387", {"start": v(-308.1, -174.55) * mm, "end": v(-308.1, -176.05) * mm});
            skLineSegment(sketch, "E388", {"start": v(-305.5, -174.55) * mm, "end": v(-308.1, -174.55) * mm});
            skLineSegment(sketch, "E389", {"start": v(-305.5, -176.05) * mm, "end": v(-305.5, -174.55) * mm});
            skLineSegment(sketch, "E390", {"start": v(-299.1, -176.05) * mm, "end": v(-305.5, -176.05) * mm});
            skLineSegment(sketch, "E391", {"start": v(-299.1, -138.25) * mm, "end": v(-299.1, -176.05) * mm});
            skLineSegment(sketch, "E392", {"start": v(-296.1, -138.25) * mm, "end": v(-299.1, -138.25) * mm});
            skLineSegment(sketch, "E393", {"start": v(-296.1, -128.25) * mm, "end": v(-296.1, -138.25) * mm});
            skLineSegment(sketch, "E394", {"start": v(-299.1, -128.25) * mm, "end": v(-296.1, -128.25) * mm});
            skLineSegment(sketch, "E395", {"start": v(-299.1, -78.25) * mm, "end": v(-299.1, -128.25) * mm});
            skLineSegment(sketch, "E396", {"start": v(-296.1, -78.25) * mm, "end": v(-299.1, -78.25) * mm});
            skLineSegment(sketch, "E397", {"start": v(-296.1, -68.25) * mm, "end": v(-296.1, -78.25) * mm});
            skLineSegment(sketch, "E398", {"start": v(-299.1, -68.25) * mm, "end": v(-296.1, -68.25) * mm});
            skLineSegment(sketch, "E399", {"start": v(-299.1, -58.45) * mm, "end": v(-299.1, -68.25) * mm});
            skLineSegment(sketch, "E400", {"start": v(-305.5, -58.45) * mm, "end": v(-299.1, -58.45) * mm});
            skLineSegment(sketch, "E401", {"start": v(-305.5, -59.95) * mm, "end": v(-305.5, -58.45) * mm});
            skLineSegment(sketch, "E402", {"start": v(-308.1, -59.95) * mm, "end": v(-305.5, -59.95) * mm});
            skLineSegment(sketch, "E403", {"start": v(-308.1, -58.45) * mm, "end": v(-308.1, -59.95) * mm});
            skLineSegment(sketch, "E404", {"start": v(-313.1, -58.45) * mm, "end": v(-308.1, -58.45) * mm});
            skLineSegment(sketch, "E405", {"start": v(-313.1, -55.05) * mm, "end": v(-313.1, -58.45) * mm});
            skLineSegment(sketch, "E406", {"start": v(-308.1, -55.05) * mm, "end": v(-313.1, -55.05) * mm});
            skLineSegment(sketch, "E407", {"start": v(-308.1, -53.55) * mm, "end": v(-308.1, -55.05) * mm});
            skLineSegment(sketch, "E408", {"start": v(-305.5, -53.55) * mm, "end": v(-308.1, -53.55) * mm});
            skLineSegment(sketch, "E409", {"start": v(-305.5, -55.05) * mm, "end": v(-305.5, -53.55) * mm});
            skLineSegment(sketch, "E410", {"start": v(-299.1, -55.05) * mm, "end": v(-305.5, -55.05) * mm});
            skLineSegment(sketch, "E411", {"start": v(-299.1, -16.25) * mm, "end": v(-299.1, -55.05) * mm});
            skLineSegment(sketch, "E412", {"start": v(-296.1, -16.25) * mm, "end": v(-299.1, -16.25) * mm});
            skLineSegment(sketch, "E413", {"start": v(-296.1, -6.25) * mm, "end": v(-296.1, -16.25) * mm});
            skLineSegment(sketch, "E414", {"start": v(-299.1, -6.25) * mm, "end": v(-296.1, -6.25) * mm});
            skLineSegment(sketch, "E415", {"start": v(-299.1, 33.55) * mm, "end": v(-299.1, -6.25) * mm});
            skLineSegment(sketch, "E416", {"start": v(-305.5, 33.55) * mm, "end": v(-299.1, 33.55) * mm});
            skLineSegment(sketch, "E417", {"start": v(-305.5, 33.55) * mm, "end": v(-305.5, 32.05) * mm});
            skLineSegment(sketch, "E418", {"start": v(-308.1, 32.05) * mm, "end": v(-305.5, 32.05) * mm});
            skLineSegment(sketch, "E419", {"start": v(-308.1, 33.55) * mm, "end": v(-308.1, 32.05) * mm});
            skLineSegment(sketch, "E420", {"start": v(-313.1, 33.55) * mm, "end": v(-308.1, 33.55) * mm});
            skLineSegment(sketch, "E421", {"start": v(-313.1, 36.95) * mm, "end": v(-313.1, 33.55) * mm});
            skLineSegment(sketch, "E422", {"start": v(-308.1, 36.95) * mm, "end": v(-313.1, 36.95) * mm});
            skLineSegment(sketch, "E423", {"start": v(-308.1, 38.45) * mm, "end": v(-308.1, 36.95) * mm});
            skLineSegment(sketch, "E424", {"start": v(-305.5, 38.45) * mm, "end": v(-308.1, 38.45) * mm});
            skLineSegment(sketch, "E425", {"start": v(-305.5, 38.45) * mm, "end": v(-305.5, 36.95) * mm});
            skLineSegment(sketch, "E426", {"start": v(-299.1, 36.95) * mm, "end": v(-305.5, 36.95) * mm});
            skLineSegment(sketch, "E427", {"start": v(-299.1, 45.75) * mm, "end": v(-299.1, 36.95) * mm});
            skLineSegment(sketch, "E428", {"start": v(-296.1, 45.75) * mm, "end": v(-299.1, 45.75) * mm});
            skLineSegment(sketch, "E429", {"start": v(-296.1, 55.75) * mm, "end": v(-296.1, 45.75) * mm});
            skLineSegment(sketch, "E430", {"start": v(-299.1, 55.75) * mm, "end": v(-296.1, 55.75) * mm});
            skLineSegment(sketch, "E431", {"start": v(-299.1, 105.75) * mm, "end": v(-299.1, 55.75) * mm});
            skLineSegment(sketch, "E432", {"start": v(-296.1, 105.75) * mm, "end": v(-299.1, 105.75) * mm});
            skLineSegment(sketch, "E433", {"start": v(-296.1, 115.75) * mm, "end": v(-296.1, 105.75) * mm});
            skLineSegment(sketch, "E434", {"start": v(-299.1, 115.75) * mm, "end": v(-296.1, 115.75) * mm});
            skLineSegment(sketch, "E435", {"start": v(-299.1, 124.55) * mm, "end": v(-299.1, 115.75) * mm});
            skLineSegment(sketch, "E436", {"start": v(-305.5, 124.55) * mm, "end": v(-299.1, 124.55) * mm});
            skLineSegment(sketch, "E437", {"start": v(-305.5, 123.05) * mm, "end": v(-305.5, 124.55) * mm});
            skLineSegment(sketch, "E438", {"start": v(-308.1, 123.05) * mm, "end": v(-305.5, 123.05) * mm});
            skLineSegment(sketch, "E439", {"start": v(-308.1, 124.55) * mm, "end": v(-308.1, 123.05) * mm});
            skLineSegment(sketch, "E440", {"start": v(-313.1, 124.55) * mm, "end": v(-308.1, 124.55) * mm});
            skLineSegment(sketch, "E441", {"start": v(-313.1, 127.95) * mm, "end": v(-313.1, 124.55) * mm});
            skLineSegment(sketch, "E442", {"start": v(-308.1, 127.95) * mm, "end": v(-313.1, 127.95) * mm});
            skLineSegment(sketch, "E443", {"start": v(-308.1, 129.45) * mm, "end": v(-308.1, 127.95) * mm});
            skLineSegment(sketch, "E444", {"start": v(-305.5, 129.45) * mm, "end": v(-308.1, 129.45) * mm});
            skLineSegment(sketch, "E445", {"start": v(-305.5, 127.95) * mm, "end": v(-305.5, 129.45) * mm});
            skLineSegment(sketch, "E446", {"start": v(-299.1, 127.95) * mm, "end": v(-305.5, 127.95) * mm});
            skLineSegment(sketch, "E447", {"start": v(-299.1, 181.25) * mm, "end": v(-299.1, 127.95) * mm});
            skLineSegment(sketch, "E448", {"start": v(-296.1, 181.25) * mm, "end": v(-299.1, 181.25) * mm});
            skLineSegment(sketch, "E449", {"start": v(-296.1, 201.25) * mm, "end": v(-296.1, 181.25) * mm});
            skLineSegment(sketch, "E450", {"start": v(-299.1, 201.25) * mm, "end": v(-296.1, 201.25) * mm});
            skArc(sketch, "E451", {"start": v(-309.1, 211.25) * mm, "mid": v(-302.03, 208.32) * mm, "end": v(-299.1, 201.25) * mm});
            skLineSegment(sketch, "E452", {"start": v(-309.1, 214.25) * mm, "end": v(-309.1, 211.25) * mm});
            skLineSegment(sketch, "E453", {"start": v(-327.6, 214.25) * mm, "end": v(-309.1, 214.25) * mm});
            skLineSegment(sketch, "E454", {"start": v(-327.6, 211.25) * mm, "end": v(-327.6, 214.25) * mm});
            skLineSegment(sketch, "E455", {"start": v(-350.9, 211.25) * mm, "end": v(-327.6, 211.25) * mm});
            skLineSegment(sketch, "E456", {"start": v(-350.9, 204.85) * mm, "end": v(-350.9, 211.25) * mm});
            skLineSegment(sketch, "E457", {"start": v(-349.4, 204.85) * mm, "end": v(-350.9, 204.85) * mm});
            skLineSegment(sketch, "E458", {"start": v(-349.4, 202.25) * mm, "end": v(-349.4, 204.85) * mm});
            skLineSegment(sketch, "E459", {"start": v(-350.9, 202.25) * mm, "end": v(-349.4, 202.25) * mm});
            skLineSegment(sketch, "E460", {"start": v(-350.9, 197.25) * mm, "end": v(-350.9, 202.25) * mm});
            skLineSegment(sketch, "E461", {"start": v(-354.3, 197.25) * mm, "end": v(-350.9, 197.25) * mm});
            skLineSegment(sketch, "E462", {"start": v(-354.3, 202.25) * mm, "end": v(-354.3, 197.25) * mm});
            skLineSegment(sketch, "E463", {"start": v(-355.8, 202.25) * mm, "end": v(-354.3, 202.25) * mm});
            skLineSegment(sketch, "E464", {"start": v(-355.8, 204.85) * mm, "end": v(-355.8, 202.25) * mm});
            skLineSegment(sketch, "E465", {"start": v(-354.3, 204.85) * mm, "end": v(-355.8, 204.85) * mm});
            skLineSegment(sketch, "E466", {"start": v(-354.3, 211.25) * mm, "end": v(-354.3, 204.85) * mm});
            skLineSegment(sketch, "E467", {"start": v(-377.6, 211.25) * mm, "end": v(-354.3, 211.25) * mm});
            skLineSegment(sketch, "E468", {"start": v(-377.6, 214.25) * mm, "end": v(-377.6, 211.25) * mm});
            skLineSegment(sketch, "E469", {"start": v(-387.6, 214.25) * mm, "end": v(-377.6, 214.25) * mm});
            skLineSegment(sketch, "E470", {"start": v(-387.6, 211.25) * mm, "end": v(-387.6, 214.25) * mm});
            skLineSegment(sketch, "E471", {"start": v(-437.6, 211.25) * mm, "end": v(-387.6, 211.25) * mm});
            skLineSegment(sketch, "E472", {"start": v(-437.6, 214.25) * mm, "end": v(-437.6, 211.25) * mm});
            skLineSegment(sketch, "E473", {"start": v(-447.6, 214.25) * mm, "end": v(-437.6, 214.25) * mm});
            skLineSegment(sketch, "E474", {"start": v(-447.6, 211.25) * mm, "end": v(-447.6, 214.25) * mm});
            skLineSegment(sketch, "E475", {"start": v(-451.9, 211.25) * mm, "end": v(-447.6, 211.25) * mm});
            skLineSegment(sketch, "E476", {"start": v(-451.9, 204.85) * mm, "end": v(-451.9, 211.25) * mm});
            skLineSegment(sketch, "E477", {"start": v(-450.4, 204.85) * mm, "end": v(-451.9, 204.85) * mm});
            skLineSegment(sketch, "E478", {"start": v(-450.4, 202.25) * mm, "end": v(-450.4, 204.85) * mm});
            skLineSegment(sketch, "E479", {"start": v(-450.4, 202.25) * mm, "end": v(-451.9, 202.25) * mm});
            skLineSegment(sketch, "E480", {"start": v(-451.9, 197.25) * mm, "end": v(-451.9, 202.25) * mm});
            skLineSegment(sketch, "E481", {"start": v(-455.3, 197.25) * mm, "end": v(-451.9, 197.25) * mm});
            skLineSegment(sketch, "E482", {"start": v(-455.3, 202.25) * mm, "end": v(-455.3, 197.25) * mm});
            skLineSegment(sketch, "E483", {"start": v(-455.3, 202.25) * mm, "end": v(-456.8, 202.25) * mm});
            skLineSegment(sketch, "E484", {"start": v(-456.8, 204.85) * mm, "end": v(-456.8, 202.25) * mm});
            skLineSegment(sketch, "E485", {"start": v(-455.3, 204.85) * mm, "end": v(-456.8, 204.85) * mm});
            skLineSegment(sketch, "E486", {"start": v(-455.3, 211.25) * mm, "end": v(-455.3, 204.85) * mm});
            skLineSegment(sketch, "E487", {"start": v(-499.6, 211.25) * mm, "end": v(-455.3, 211.25) * mm});
            skLineSegment(sketch, "E488", {"start": v(-499.6, 214.25) * mm, "end": v(-499.6, 211.25) * mm});
            skLineSegment(sketch, "E489", {"start": v(-509.6, 214.25) * mm, "end": v(-499.6, 214.25) * mm});
            skLineSegment(sketch, "E490", {"start": v(-509.6, 211.25) * mm, "end": v(-509.6, 214.25) * mm});
            skLineSegment(sketch, "E491", {"start": v(-553.9, 211.25) * mm, "end": v(-509.6, 211.25) * mm});
            skLineSegment(sketch, "E492", {"start": v(-553.9, 204.85) * mm, "end": v(-553.9, 211.25) * mm});
            skLineSegment(sketch, "E493", {"start": v(-553.9, 204.85) * mm, "end": v(-552.4, 204.85) * mm});
            skLineSegment(sketch, "E494", {"start": v(-552.4, 202.25) * mm, "end": v(-552.4, 204.85) * mm});
            skLineSegment(sketch, "E495", {"start": v(-553.9, 202.25) * mm, "end": v(-552.4, 202.25) * mm});
            skLineSegment(sketch, "E496", {"start": v(-553.9, 197.25) * mm, "end": v(-553.9, 202.25) * mm});
            skLineSegment(sketch, "E497", {"start": v(-557.3, 197.25) * mm, "end": v(-553.9, 197.25) * mm});
            skLineSegment(sketch, "E498", {"start": v(-557.3, 202.25) * mm, "end": v(-557.3, 197.25) * mm});
            skLineSegment(sketch, "E499", {"start": v(-558.8, 202.25) * mm, "end": v(-557.3, 202.25) * mm});
            skLineSegment(sketch, "E500", {"start": v(-558.8, 204.85) * mm, "end": v(-558.8, 202.25) * mm});
            skLineSegment(sketch, "E501", {"start": v(-558.8, 204.85) * mm, "end": v(-557.3, 204.85) * mm});
            skLineSegment(sketch, "E502", {"start": v(-557.3, 211.25) * mm, "end": v(-557.3, 204.85) * mm});
            skLineSegment(sketch, "E503", {"start": v(-561.6, 211.25) * mm, "end": v(-557.3, 211.25) * mm});
            skLineSegment(sketch, "E504", {"start": v(-561.6, 214.25) * mm, "end": v(-561.6, 211.25) * mm});
            skLineSegment(sketch, "E505", {"start": v(-571.6, 214.25) * mm, "end": v(-561.6, 214.25) * mm});
            skLineSegment(sketch, "E506", {"start": v(-571.6, 211.25) * mm, "end": v(-571.6, 214.25) * mm});
            skLineSegment(sketch, "E507", {"start": v(-621.6, 211.25) * mm, "end": v(-571.6, 211.25) * mm});
            skLineSegment(sketch, "E508", {"start": v(-621.6, 214.25) * mm, "end": v(-621.6, 211.25) * mm});
            skLineSegment(sketch, "E509", {"start": v(-631.6, 214.25) * mm, "end": v(-621.6, 214.25) * mm});
            skLineSegment(sketch, "E510", {"start": v(-631.6, 211.25) * mm, "end": v(-631.6, 214.25) * mm});
            skLineSegment(sketch, "E511", {"start": v(-654.9, 211.25) * mm, "end": v(-631.6, 211.25) * mm});
            skLineSegment(sketch, "E512", {"start": v(-654.9, 204.85) * mm, "end": v(-654.9, 211.25) * mm});
            skLineSegment(sketch, "E513", {"start": v(-653.4, 204.85) * mm, "end": v(-654.9, 204.85) * mm});
            skLineSegment(sketch, "E514", {"start": v(-653.4, 202.25) * mm, "end": v(-653.4, 204.85) * mm});
            skLineSegment(sketch, "E515", {"start": v(-654.9, 202.25) * mm, "end": v(-653.4, 202.25) * mm});
            skLineSegment(sketch, "E516", {"start": v(-654.9, 197.25) * mm, "end": v(-654.9, 202.25) * mm});
            skLineSegment(sketch, "E517", {"start": v(-658.3, 197.25) * mm, "end": v(-654.9, 197.25) * mm});
            skLineSegment(sketch, "E518", {"start": v(-658.3, 202.25) * mm, "end": v(-658.3, 197.25) * mm});
            skLineSegment(sketch, "E519", {"start": v(-659.8, 202.25) * mm, "end": v(-658.3, 202.25) * mm});
            skLineSegment(sketch, "E520", {"start": v(-659.8, 204.85) * mm, "end": v(-659.8, 202.25) * mm});
            skLineSegment(sketch, "E521", {"start": v(-658.3, 204.85) * mm, "end": v(-659.8, 204.85) * mm});
            skLineSegment(sketch, "E522", {"start": v(-658.3, 211.25) * mm, "end": v(-658.3, 204.85) * mm});
            skLineSegment(sketch, "E523", {"start": v(-681.6, 211.25) * mm, "end": v(-658.3, 211.25) * mm});
            skLineSegment(sketch, "E524", {"start": v(-681.6, 214.25) * mm, "end": v(-681.6, 211.25) * mm});
            skLineSegment(sketch, "E525", {"start": v(-700.1, 214.25) * mm, "end": v(-681.6, 214.25) * mm});
            skLineSegment(sketch, "E526", {"start": v(-700.1, 211.25) * mm, "end": v(-700.1, 214.25) * mm});
            skArc(sketch, "E527", {"start": v(-710.1, 201.25) * mm, "mid": v(-707.17, 208.32) * mm, "end": v(-700.1, 211.25) * mm});
            skLineSegment(sketch, "E528", {"start": v(-713.1, 201.25) * mm, "end": v(-710.1, 201.25) * mm});
            skLineSegment(sketch, "E529", {"start": v(-713.1, 181.25) * mm, "end": v(-713.1, 201.25) * mm});
            skLineSegment(sketch, "E530", {"start": v(-710.1, 181.25) * mm, "end": v(-713.1, 181.25) * mm});
            skLineSegment(sketch, "E531", {"start": v(-710.1, 127.95) * mm, "end": v(-710.1, 181.25) * mm});
            skLineSegment(sketch, "E532", {"start": v(-703.7, 127.95) * mm, "end": v(-710.1, 127.95) * mm});
            skLineSegment(sketch, "E533", {"start": v(-703.7, 129.45) * mm, "end": v(-703.7, 127.95) * mm});
            skLineSegment(sketch, "E534", {"start": v(-701.1, 129.45) * mm, "end": v(-703.7, 129.45) * mm});
            skLineSegment(sketch, "E535", {"start": v(-701.1, 127.95) * mm, "end": v(-701.1, 129.45) * mm});
            skLineSegment(sketch, "E536", {"start": v(-696.1, 127.95) * mm, "end": v(-701.1, 127.95) * mm});
            skLineSegment(sketch, "E537", {"start": v(-696.1, 124.55) * mm, "end": v(-696.1, 127.95) * mm});
            skLineSegment(sketch, "E538", {"start": v(-701.1, 124.55) * mm, "end": v(-696.1, 124.55) * mm});
            skLineSegment(sketch, "E539", {"start": v(-701.1, 123.05) * mm, "end": v(-701.1, 124.55) * mm});
            skLineSegment(sketch, "E540", {"start": v(-703.7, 123.05) * mm, "end": v(-701.1, 123.05) * mm});
            skLineSegment(sketch, "E541", {"start": v(-703.7, 124.55) * mm, "end": v(-703.7, 123.05) * mm});
            skLineSegment(sketch, "E542", {"start": v(-710.1, 124.55) * mm, "end": v(-703.7, 124.55) * mm});
            skLineSegment(sketch, "E543", {"start": v(-710.1, 115.75) * mm, "end": v(-710.1, 124.55) * mm});
            skLineSegment(sketch, "E544", {"start": v(-713.1, 115.75) * mm, "end": v(-710.1, 115.75) * mm});
            skLineSegment(sketch, "E545", {"start": v(-713.1, 105.75) * mm, "end": v(-713.1, 115.75) * mm});
            skLineSegment(sketch, "E546", {"start": v(-710.1, 105.75) * mm, "end": v(-713.1, 105.75) * mm});
            skLineSegment(sketch, "E547", {"start": v(-710.1, 55.75) * mm, "end": v(-710.1, 105.75) * mm});
            skLineSegment(sketch, "E548", {"start": v(-713.1, 55.75) * mm, "end": v(-710.1, 55.75) * mm});
            skLineSegment(sketch, "E549", {"start": v(-713.1, 45.75) * mm, "end": v(-713.1, 55.75) * mm});
            skLineSegment(sketch, "E550", {"start": v(-710.1, 45.75) * mm, "end": v(-713.1, 45.75) * mm});
            skLineSegment(sketch, "E551", {"start": v(-710.1, 36.95) * mm, "end": v(-710.1, 45.75) * mm});
            skLineSegment(sketch, "E552", {"start": v(-703.7, 36.95) * mm, "end": v(-710.1, 36.95) * mm});
            skLineSegment(sketch, "E553", {"start": v(-703.7, 38.45) * mm, "end": v(-703.7, 36.95) * mm});
            skLineSegment(sketch, "E554", {"start": v(-701.1, 38.45) * mm, "end": v(-703.7, 38.45) * mm});
            skLineSegment(sketch, "E555", {"start": v(-701.1, 38.45) * mm, "end": v(-701.1, 36.95) * mm});
            skLineSegment(sketch, "E556", {"start": v(-696.1, 36.95) * mm, "end": v(-701.1, 36.95) * mm});
            skLineSegment(sketch, "E557", {"start": v(-696.1, 33.55) * mm, "end": v(-696.1, 36.95) * mm});
            skLineSegment(sketch, "E558", {"start": v(-701.1, 33.55) * mm, "end": v(-696.1, 33.55) * mm});
            skLineSegment(sketch, "E559", {"start": v(-701.1, 33.55) * mm, "end": v(-701.1, 32.05) * mm});
            skLineSegment(sketch, "E560", {"start": v(-703.7, 32.05) * mm, "end": v(-701.1, 32.05) * mm});
            skLineSegment(sketch, "E561", {"start": v(-703.7, 33.55) * mm, "end": v(-703.7, 32.05) * mm});
            skLineSegment(sketch, "E562", {"start": v(-710.1, 33.55) * mm, "end": v(-703.7, 33.55) * mm});
            skLineSegment(sketch, "E563", {"start": v(-710.1, -6.25) * mm, "end": v(-710.1, 33.55) * mm});
            skLineSegment(sketch, "E564", {"start": v(-713.1, -6.25) * mm, "end": v(-710.1, -6.25) * mm});
            skLineSegment(sketch, "E565", {"start": v(-713.1, -16.25) * mm, "end": v(-713.1, -6.25) * mm});
            skLineSegment(sketch, "E566", {"start": v(-710.1, -16.25) * mm, "end": v(-713.1, -16.25) * mm});
            skLineSegment(sketch, "E567", {"start": v(-710.1, -55.05) * mm, "end": v(-710.1, -16.25) * mm});
            skLineSegment(sketch, "E568", {"start": v(-703.7, -55.05) * mm, "end": v(-710.1, -55.05) * mm});
            skLineSegment(sketch, "E569", {"start": v(-703.7, -53.55) * mm, "end": v(-703.7, -55.05) * mm});
            skLineSegment(sketch, "E570", {"start": v(-701.1, -53.55) * mm, "end": v(-703.7, -53.55) * mm});
            skLineSegment(sketch, "E571", {"start": v(-701.1, -55.05) * mm, "end": v(-701.1, -53.55) * mm});
            skLineSegment(sketch, "E572", {"start": v(-696.1, -55.05) * mm, "end": v(-701.1, -55.05) * mm});
            skLineSegment(sketch, "E573", {"start": v(-696.1, -58.45) * mm, "end": v(-696.1, -55.05) * mm});
            skLineSegment(sketch, "E574", {"start": v(-701.1, -58.45) * mm, "end": v(-696.1, -58.45) * mm});
            skLineSegment(sketch, "E575", {"start": v(-701.1, -59.95) * mm, "end": v(-701.1, -58.45) * mm});
            skLineSegment(sketch, "E576", {"start": v(-703.7, -59.95) * mm, "end": v(-701.1, -59.95) * mm});
            skLineSegment(sketch, "E577", {"start": v(-703.7, -58.45) * mm, "end": v(-703.7, -59.95) * mm});
            skLineSegment(sketch, "E578", {"start": v(-710.1, -58.45) * mm, "end": v(-703.7, -58.45) * mm});
            skLineSegment(sketch, "E579", {"start": v(-710.1, -68.25) * mm, "end": v(-710.1, -58.45) * mm});
            skLineSegment(sketch, "E580", {"start": v(-713.1, -68.25) * mm, "end": v(-710.1, -68.25) * mm});
            skLineSegment(sketch, "E581", {"start": v(-713.1, -78.25) * mm, "end": v(-713.1, -68.25) * mm});
            skLineSegment(sketch, "E582", {"start": v(-710.1, -78.25) * mm, "end": v(-713.1, -78.25) * mm});
            skLineSegment(sketch, "E583", {"start": v(-710.1, -128.25) * mm, "end": v(-710.1, -78.25) * mm});
            skLineSegment(sketch, "E584", {"start": v(-713.1, -128.25) * mm, "end": v(-710.1, -128.25) * mm});
            skLineSegment(sketch, "E585", {"start": v(-713.1, -138.25) * mm, "end": v(-713.1, -128.25) * mm});
            skLineSegment(sketch, "E586", {"start": v(-710.1, -138.25) * mm, "end": v(-713.1, -138.25) * mm});
            skLineSegment(sketch, "E587", {"start": v(-710.1, -176.05) * mm, "end": v(-710.1, -138.25) * mm});
            skLineSegment(sketch, "E588", {"start": v(-703.7, -176.05) * mm, "end": v(-710.1, -176.05) * mm});
            skLineSegment(sketch, "E589", {"start": v(-703.7, -174.55) * mm, "end": v(-703.7, -176.05) * mm});
            skLineSegment(sketch, "E590", {"start": v(-701.1, -174.55) * mm, "end": v(-703.7, -174.55) * mm});
            skLineSegment(sketch, "E591", {"start": v(-701.1, -176.05) * mm, "end": v(-701.1, -174.55) * mm});
            skLineSegment(sketch, "E592", {"start": v(-696.1, -176.05) * mm, "end": v(-701.1, -176.05) * mm});
            skLineSegment(sketch, "E593", {"start": v(-696.1, -179.45) * mm, "end": v(-696.1, -176.05) * mm});
            skLineSegment(sketch, "E594", {"start": v(-701.1, -179.45) * mm, "end": v(-696.1, -179.45) * mm});
            skLineSegment(sketch, "E595", {"start": v(-701.1, -180.95) * mm, "end": v(-701.1, -179.45) * mm});
            skLineSegment(sketch, "E596", {"start": v(-703.7, -180.95) * mm, "end": v(-701.1, -180.95) * mm});
            skLineSegment(sketch, "E597", {"start": v(-703.7, -179.45) * mm, "end": v(-703.7, -180.95) * mm});
            skLineSegment(sketch, "E598", {"start": v(-710.1, -179.45) * mm, "end": v(-703.7, -179.45) * mm});
            skLineSegment(sketch, "E599", {"start": v(-710.1, -188.25) * mm, "end": v(-710.1, -179.45) * mm});
            skLineSegment(sketch, "E600", {"start": v(-713.1, -188.25) * mm, "end": v(-710.1, -188.25) * mm});
            skLineSegment(sketch, "E601", {"start": v(-713.1, -201.25) * mm, "end": v(-713.1, -188.25) * mm});
            skLineSegment(sketch, "E602", {"start": v(-710.1, -201.25) * mm, "end": v(-713.1, -201.25) * mm});
            skArc(sketch, "E603", {"start": v(-710.1, -201.25) * mm, "mid": v(-707.17, -208.32) * mm, "end": v(-700.1, -211.25) * mm});
            skLineSegment(sketch, "E604", {"start": v(-700.1, -214.25) * mm, "end": v(-700.1, -211.25) * mm});
            skLineSegment(sketch, "E605", {"start": v(-681.6, -214.25) * mm, "end": v(-700.1, -214.25) * mm});
            skLineSegment(sketch, "E606", {"start": v(-681.6, -211.25) * mm, "end": v(-681.6, -214.25) * mm});
            skLineSegment(sketch, "E607", {"start": v(-658.3, -211.25) * mm, "end": v(-681.6, -211.25) * mm});
            skLineSegment(sketch, "E608", {"start": v(-658.3, -208.35) * mm, "end": v(-658.3, -211.25) * mm});
            skLineSegment(sketch, "E609", {"start": v(-659.8, -208.35) * mm, "end": v(-658.3, -208.35) * mm});
            skLineSegment(sketch, "E610", {"start": v(-659.8, -205.75) * mm, "end": v(-659.8, -208.35) * mm});
            skLineSegment(sketch, "E611", {"start": v(-658.3, -205.75) * mm, "end": v(-659.8, -205.75) * mm});
            skLineSegment(sketch, "E612", {"start": v(-658.3, -202.75) * mm, "end": v(-658.3, -205.75) * mm});
            skLineSegment(sketch, "E613", {"start": v(-654.9, -202.75) * mm, "end": v(-658.3, -202.75) * mm});
            skLineSegment(sketch, "E614", {"start": v(-654.9, -205.75) * mm, "end": v(-654.9, -202.75) * mm});
            skLineSegment(sketch, "E615", {"start": v(-653.4, -205.75) * mm, "end": v(-654.9, -205.75) * mm});
            skLineSegment(sketch, "E616", {"start": v(-653.4, -208.35) * mm, "end": v(-653.4, -205.75) * mm});
            skLineSegment(sketch, "E617", {"start": v(-654.9, -208.35) * mm, "end": v(-653.4, -208.35) * mm});
            skLineSegment(sketch, "E618", {"start": v(-654.9, -211.25) * mm, "end": v(-654.9, -208.35) * mm});
            skLineSegment(sketch, "E619", {"start": v(-631.6, -211.25) * mm, "end": v(-654.9, -211.25) * mm});
            skLineSegment(sketch, "E620", {"start": v(-631.6, -214.25) * mm, "end": v(-631.6, -211.25) * mm});
            skLineSegment(sketch, "E621", {"start": v(-621.6, -214.25) * mm, "end": v(-631.6, -214.25) * mm});
            skLineSegment(sketch, "E622", {"start": v(-621.6, -211.25) * mm, "end": v(-621.6, -214.25) * mm});
            skLineSegment(sketch, "E623", {"start": v(-571.6, -211.25) * mm, "end": v(-621.6, -211.25) * mm});
            skLineSegment(sketch, "E624", {"start": v(-571.6, -214.25) * mm, "end": v(-571.6, -211.25) * mm});
            skLineSegment(sketch, "E625", {"start": v(-561.6, -214.25) * mm, "end": v(-571.6, -214.25) * mm});
            skLineSegment(sketch, "E626", {"start": v(-561.6, -211.25) * mm, "end": v(-561.6, -214.25) * mm});
            skLineSegment(sketch, "E627", {"start": v(-557.3, -211.25) * mm, "end": v(-561.6, -211.25) * mm});
            skLineSegment(sketch, "E628", {"start": v(-557.3, -208.35) * mm, "end": v(-557.3, -211.25) * mm});
            skLineSegment(sketch, "E629", {"start": v(-558.8, -208.35) * mm, "end": v(-557.3, -208.35) * mm});
            skLineSegment(sketch, "E630", {"start": v(-558.8, -205.75) * mm, "end": v(-558.8, -208.35) * mm});
            skLineSegment(sketch, "E631", {"start": v(-558.8, -205.75) * mm, "end": v(-557.3, -205.75) * mm});
            skLineSegment(sketch, "E632", {"start": v(-557.3, -202.75) * mm, "end": v(-557.3, -205.75) * mm});
            skLineSegment(sketch, "E633", {"start": v(-553.9, -202.75) * mm, "end": v(-557.3, -202.75) * mm});
            skLineSegment(sketch, "E634", {"start": v(-553.9, -205.75) * mm, "end": v(-553.9, -202.75) * mm});
            skLineSegment(sketch, "E635", {"start": v(-553.9, -205.75) * mm, "end": v(-552.4, -205.75) * mm});
            skLineSegment(sketch, "E636", {"start": v(-552.4, -208.35) * mm, "end": v(-552.4, -205.75) * mm});
            skLineSegment(sketch, "E637", {"start": v(-553.9, -208.35) * mm, "end": v(-552.4, -208.35) * mm});
            skLineSegment(sketch, "E638", {"start": v(-553.9, -211.25) * mm, "end": v(-553.9, -208.35) * mm});
            skLineSegment(sketch, "E639", {"start": v(-509.6, -211.25) * mm, "end": v(-553.9, -211.25) * mm});
            skLineSegment(sketch, "E640", {"start": v(-509.6, -214.25) * mm, "end": v(-509.6, -211.25) * mm});
            skLineSegment(sketch, "E641", {"start": v(-499.6, -214.25) * mm, "end": v(-509.6, -214.25) * mm});
            skLineSegment(sketch, "E642", {"start": v(-499.6, -211.25) * mm, "end": v(-499.6, -214.25) * mm});
            skCircle(sketch, "E643", {"center": v(-666.6, -172.75) * mm, "radius": 3 * mm});
            skCircle(sketch, "E644", {"center": v(-666.6, 11.25) * mm, "radius": 3 * mm});
            skCircle(sketch, "E645", {"center": v(-342.6, 11.25) * mm, "radius": 3 * mm});
            skCircle(sketch, "E646", {"center": v(-342.6, -172.75) * mm, "radius": 3 * mm});
            skCircle(sketch, "E647", {"center": v(-508.1, 161.1) * mm, "radius": 10 * mm});
            skCircle(sketch, "E648", {"center": v(-612.1, 161.9) * mm, "radius": 10 * mm});
            skCircle(sketch, "E649", {"center": v(-397.1, 161.9) * mm, "radius": 10 * mm});
            skLineSegment(sketch, "E650.bottom", {"start": v(-971.73, 161.45) * mm, "end": v(-856.73, 161.45) * mm});
            skLineSegment(sketch, "E650.top", {"start": v(-971.73, -53.55) * mm, "end": v(-856.73, -53.55) * mm});
            skLineSegment(sketch, "E650.left", {"start": v(-971.73, 161.45) * mm, "end": v(-971.73, -53.55) * mm});
            skLineSegment(sketch, "E650.right", {"start": v(-856.73, 161.45) * mm, "end": v(-856.73, -53.55) * mm});
            skCircle(sketch, "E651", {"center": v(-1110.38, -101.96) * mm, "radius": 105 * mm});
            skLineSegment(sketch, "E652.bottom", {"start": v(-836.73, -78.25) * mm, "end": v(-836.73, -153.25) * mm});
            skLineSegment(sketch, "E652.top", {"start": v(-971.73, -78.25) * mm, "end": v(-971.73, -153.25) * mm});
            skLineSegment(sketch, "E652.left", {"start": v(-836.73, -78.25) * mm, "end": v(-971.73, -78.25) * mm});
            skLineSegment(sketch, "E652.right", {"start": v(-836.73, -153.25) * mm, "end": v(-971.73, -153.25) * mm});
            skLineSegment(sketch, "E653.bottom", {"start": v(-1095.32, 64.96) * mm, "end": v(-1038.92, 64.96) * mm});
            skLineSegment(sketch, "E653.top", {"start": v(-1095.32, 8.56) * mm, "end": v(-1038.92, 8.56) * mm});
            skLineSegment(sketch, "E653.left", {"start": v(-1095.32, 64.96) * mm, "end": v(-1095.32, 8.56) * mm});
            skLineSegment(sketch, "E653.right", {"start": v(-1038.92, 64.96) * mm, "end": v(-1038.92, 8.56) * mm});
            skCircle(sketch, "E654", {"center": v(-1110.38, -101.96) * mm, "radius": 30 * mm});
            skLineSegment(sketch, "E655.bottom", {"start": v(-928.33, -287.41) * mm, "end": v(-852.33, -287.41) * mm});
            skLineSegment(sketch, "E655.top", {"start": v(-928.33, -171.41) * mm, "end": v(-852.33, -171.41) * mm});
            skLineSegment(sketch, "E655.left", {"start": v(-928.33, -287.41) * mm, "end": v(-928.33, -171.41) * mm});
            skLineSegment(sketch, "E655.right", {"start": v(-852.33, -287.41) * mm, "end": v(-852.33, -171.41) * mm});
            skCircle(sketch, "E656", {"center": v(-1067.12, 36.76) * mm, "radius": 18.5 * mm});
            skPoint(sketch, "E656.centerSnap0", {"position": v(-1095.32, 36.76) * mm});
            skPoint(sketch, "E656.centerSnap1", {"position": v(-1067.12, 64.96) * mm});
            skCircle(sketch, "E657", {"center": v(-612.1, 126.9) * mm, "radius": 1.5 * mm});
            skCircle(sketch, "E658", {"center": v(-508.1, 126.1) * mm, "radius": 1.5 * mm});
            skCircle(sketch, "E659", {"center": v(-397.1, 126.9) * mm, "radius": 1.5 * mm});
            skCircle(sketch, "E660.1.0", {"center": v(-581.8, 144.4) * mm, "radius": 1.5 * mm});
            skCircle(sketch, "E660.2.0", {"center": v(-581.8, 179.4) * mm, "radius": 1.5 * mm});
            skCircle(sketch, "E660.3.0", {"center": v(-612.1, 196.9) * mm, "radius": 1.5 * mm});
            skCircle(sketch, "E660.4.0", {"center": v(-642.41, 179.4) * mm, "radius": 1.5 * mm});
            skCircle(sketch, "E660.5.0", {"center": v(-642.41, 144.4) * mm, "radius": 1.5 * mm});
            skCircle(sketch, "E661.1.0", {"center": v(-477.8, 143.6) * mm, "radius": 1.5 * mm});
            skCircle(sketch, "E661.2.0", {"center": v(-477.8, 178.6) * mm, "radius": 1.5 * mm});
            skCircle(sketch, "E661.3.0", {"center": v(-508.1, 196.1) * mm, "radius": 1.5 * mm});
            skCircle(sketch, "E661.4.0", {"center": v(-538.41, 178.6) * mm, "radius": 1.5 * mm});
            skCircle(sketch, "E661.5.0", {"center": v(-538.41, 143.6) * mm, "radius": 1.5 * mm});
            skCircle(sketch, "E662.1.0", {"center": v(-366.8, 144.4) * mm, "radius": 1.5 * mm});
            skCircle(sketch, "E662.2.0", {"center": v(-366.8, 179.4) * mm, "radius": 1.5 * mm});
            skCircle(sketch, "E662.3.0", {"center": v(-397.1, 196.9) * mm, "radius": 1.5 * mm});
            skCircle(sketch, "E662.4.0", {"center": v(-427.41, 179.4) * mm, "radius": 1.5 * mm});
            skCircle(sketch, "E662.5.0", {"center": v(-427.41, 144.4) * mm, "radius": 1.5 * mm});
            skCircle(sketch, "E663", {"center": v(-9.5, 121.25) * mm, "radius": 1.5 * mm});
            skCircle(sketch, "E664", {"center": v(98, 121.25) * mm, "radius": 1.5 * mm});
            skCircle(sketch, "E665", {"center": v(205.5, 121.25) * mm, "radius": 1.5 * mm});
            skCircle(sketch, "E666.1.0", {"center": v(20.81, 138.75) * mm, "radius": 1.5 * mm});
            skCircle(sketch, "E666.2.0", {"center": v(20.81, 173.75) * mm, "radius": 1.5 * mm});
            skCircle(sketch, "E666.3.0", {"center": v(-9.5, 191.25) * mm, "radius": 1.5 * mm});
            skCircle(sketch, "E666.4.0", {"center": v(-39.81, 173.75) * mm, "radius": 1.5 * mm});
            skCircle(sketch, "E666.5.0", {"center": v(-39.81, 138.75) * mm, "radius": 1.5 * mm});
            skPoint(sketch, "E666.center", {"position": v(-9.5, 156.25) * mm});
            skCircle(sketch, "E667.1.0", {"center": v(128.31, 138.75) * mm, "radius": 1.5 * mm});
            skCircle(sketch, "E667.2.0", {"center": v(128.31, 173.75) * mm, "radius": 1.5 * mm});
            skCircle(sketch, "E667.3.0", {"center": v(98, 191.25) * mm, "radius": 1.5 * mm});
            skCircle(sketch, "E667.4.0", {"center": v(67.69, 173.75) * mm, "radius": 1.5 * mm});
            skCircle(sketch, "E667.5.0", {"center": v(67.69, 138.75) * mm, "radius": 1.5 * mm});
            skPoint(sketch, "E667.center", {"position": v(98, 156.25) * mm});
            skCircle(sketch, "E668.1.0", {"center": v(235.81, 138.75) * mm, "radius": 1.5 * mm});
            skCircle(sketch, "E668.2.0", {"center": v(235.81, 173.75) * mm, "radius": 1.5 * mm});
            skCircle(sketch, "E668.3.0", {"center": v(205.5, 191.25) * mm, "radius": 1.5 * mm});
            skCircle(sketch, "E668.4.0", {"center": v(175.19, 173.75) * mm, "radius": 1.5 * mm});
            skCircle(sketch, "E668.5.0", {"center": v(175.19, 138.75) * mm, "radius": 1.5 * mm});
            skPoint(sketch, "E668.center", {"position": v(205.5, 156.25) * mm});
            skCircle(sketch, "E669", {"center": v(98, 156.25) * mm, "radius": 3 * mm});
            skCircle(sketch, "E670", {"center": v(205.5, 156.25) * mm, "radius": 3 * mm});
            skCircle(sketch, "E671", {"center": v(-9.5, 156.25) * mm, "radius": 3 * mm});
            skCircle(sketch, "E672", {"center": v(412.83, -56.75) * mm, "radius": 1.5 * mm});
            skCircle(sketch, "E673", {"center": v(412.83, -177.75) * mm, "radius": 1.5 * mm});
            skCircle(sketch, "E674", {"center": v(412.83, 35.25) * mm, "radius": 1.5 * mm});
            skCircle(sketch, "E675", {"center": v(412.83, 126.25) * mm, "radius": 1.5 * mm});
            skLineSegment(sketch, "E676.bottom", {"start": v(415.33, 181.25) * mm, "end": v(410.33, 181.25) * mm});
            skLineSegment(sketch, "E676.top", {"start": v(415.33, 201.25) * mm, "end": v(410.33, 201.25) * mm});
            skLineSegment(sketch, "E676.left", {"start": v(415.33, 181.25) * mm, "end": v(415.33, 201.25) * mm});
            skLineSegment(sketch, "E676.right", {"start": v(410.33, 181.25) * mm, "end": v(410.33, 201.25) * mm});
            skPoint(sketch, "E676.middle", {"position": v(412.83, 191.25) * mm});
            skLineSegment(sketch, "E677.bottom", {"start": v(410.33, 105.75) * mm, "end": v(415.33, 105.75) * mm});
            skLineSegment(sketch, "E677.top", {"start": v(410.33, 115.75) * mm, "end": v(415.33, 115.75) * mm});
            skLineSegment(sketch, "E677.left", {"start": v(410.33, 105.75) * mm, "end": v(410.33, 115.75) * mm});
            skLineSegment(sketch, "E677.right", {"start": v(415.33, 105.75) * mm, "end": v(415.33, 115.75) * mm});
            skPoint(sketch, "E677.middle", {"position": v(412.83, 110.75) * mm});
            skLineSegment(sketch, "E678.bottom", {"start": v(410.33, 45.75) * mm, "end": v(415.33, 45.75) * mm});
            skLineSegment(sketch, "E678.top", {"start": v(410.33, 55.75) * mm, "end": v(415.33, 55.75) * mm});
            skLineSegment(sketch, "E678.left", {"start": v(410.33, 45.75) * mm, "end": v(410.33, 55.75) * mm});
            skLineSegment(sketch, "E678.right", {"start": v(415.33, 45.75) * mm, "end": v(415.33, 55.75) * mm});
            skPoint(sketch, "E678.middle", {"position": v(412.83, 50.75) * mm});
            skLineSegment(sketch, "E679.bottom", {"start": v(410.33, -16.25) * mm, "end": v(415.33, -16.25) * mm});
            skLineSegment(sketch, "E679.top", {"start": v(410.33, -6.25) * mm, "end": v(415.33, -6.25) * mm});
            skLineSegment(sketch, "E679.left", {"start": v(410.33, -16.25) * mm, "end": v(410.33, -6.25) * mm});
            skLineSegment(sketch, "E679.right", {"start": v(415.33, -16.25) * mm, "end": v(415.33, -6.25) * mm});
            skPoint(sketch, "E679.middle", {"position": v(412.83, -11.25) * mm});
            skLineSegment(sketch, "E680.bottom", {"start": v(410.33, -78.25) * mm, "end": v(415.33, -78.25) * mm});
            skLineSegment(sketch, "E680.top", {"start": v(410.33, -68.25) * mm, "end": v(415.33, -68.25) * mm});
            skLineSegment(sketch, "E680.left", {"start": v(410.33, -78.25) * mm, "end": v(410.33, -68.25) * mm});
            skLineSegment(sketch, "E680.right", {"start": v(415.33, -78.25) * mm, "end": v(415.33, -68.25) * mm});
            skPoint(sketch, "E680.middle", {"position": v(412.83, -73.25) * mm});
            skLineSegment(sketch, "E681.bottom", {"start": v(410.33, -138.25) * mm, "end": v(415.33, -138.25) * mm});
            skLineSegment(sketch, "E681.top", {"start": v(410.33, -128.25) * mm, "end": v(415.33, -128.25) * mm});
            skLineSegment(sketch, "E681.left", {"start": v(410.33, -138.25) * mm, "end": v(410.33, -128.25) * mm});
            skLineSegment(sketch, "E681.right", {"start": v(415.33, -138.25) * mm, "end": v(415.33, -128.25) * mm});
            skPoint(sketch, "E681.middle", {"position": v(412.83, -133.25) * mm});
            skLineSegment(sketch, "E682.bottom", {"start": v(410.33, -201.25) * mm, "end": v(415.33, -201.25) * mm});
            skLineSegment(sketch, "E682.top", {"start": v(410.33, -188.25) * mm, "end": v(415.33, -188.25) * mm});
            skLineSegment(sketch, "E682.left", {"start": v(410.33, -201.25) * mm, "end": v(410.33, -188.25) * mm});
            skLineSegment(sketch, "E682.right", {"start": v(415.33, -201.25) * mm, "end": v(415.33, -188.25) * mm});
            skPoint(sketch, "E682.middle", {"position": v(412.83, -194.75) * mm});
            skCircle(sketch, "E683", {"center": v(535.6, -56.75) * mm, "radius": 1.5 * mm});
            skCircle(sketch, "E684", {"center": v(535.6, -177.75) * mm, "radius": 1.5 * mm});
            skCircle(sketch, "E685", {"center": v(535.6, 35.25) * mm, "radius": 1.5 * mm});
            skCircle(sketch, "E686", {"center": v(535.6, 126.25) * mm, "radius": 1.5 * mm});
            skLineSegment(sketch, "E687.bottom", {"start": v(537.1, 181.25) * mm, "end": v(534.1, 181.25) * mm});
            skLineSegment(sketch, "E687.top", {"start": v(537.1, 201.25) * mm, "end": v(534.1, 201.25) * mm});
            skLineSegment(sketch, "E687.left", {"start": v(537.1, 181.25) * mm, "end": v(537.1, 201.25) * mm});
            skLineSegment(sketch, "E687.right", {"start": v(534.1, 181.25) * mm, "end": v(534.1, 201.25) * mm});
            skPoint(sketch, "E687.middle", {"position": v(535.6, 191.25) * mm});
            skLineSegment(sketch, "E688.bottom", {"start": v(534.1, 105.75) * mm, "end": v(537.1, 105.75) * mm});
            skLineSegment(sketch, "E688.top", {"start": v(534.1, 115.75) * mm, "end": v(537.1, 115.75) * mm});
            skLineSegment(sketch, "E688.left", {"start": v(534.1, 105.75) * mm, "end": v(534.1, 115.75) * mm});
            skLineSegment(sketch, "E688.right", {"start": v(537.1, 105.75) * mm, "end": v(537.1, 115.75) * mm});
            skPoint(sketch, "E688.middle", {"position": v(535.6, 110.75) * mm});
            skLineSegment(sketch, "E689.bottom", {"start": v(534.1, 45.75) * mm, "end": v(537.1, 45.75) * mm});
            skLineSegment(sketch, "E689.top", {"start": v(534.1, 55.75) * mm, "end": v(537.1, 55.75) * mm});
            skLineSegment(sketch, "E689.left", {"start": v(534.1, 45.75) * mm, "end": v(534.1, 55.75) * mm});
            skLineSegment(sketch, "E689.right", {"start": v(537.1, 45.75) * mm, "end": v(537.1, 55.75) * mm});
            skPoint(sketch, "E689.middle", {"position": v(535.6, 50.75) * mm});
            skLineSegment(sketch, "E690.bottom", {"start": v(534.1, -16.25) * mm, "end": v(537.1, -16.25) * mm});
            skLineSegment(sketch, "E690.top", {"start": v(534.1, -6.25) * mm, "end": v(537.1, -6.25) * mm});
            skLineSegment(sketch, "E690.left", {"start": v(534.1, -16.25) * mm, "end": v(534.1, -6.25) * mm});
            skLineSegment(sketch, "E690.right", {"start": v(537.1, -16.25) * mm, "end": v(537.1, -6.25) * mm});
            skPoint(sketch, "E690.middle", {"position": v(535.6, -11.25) * mm});
            skLineSegment(sketch, "E691.bottom", {"start": v(534.1, -78.25) * mm, "end": v(537.1, -78.25) * mm});
            skLineSegment(sketch, "E691.top", {"start": v(534.1, -68.25) * mm, "end": v(537.1, -68.25) * mm});
            skLineSegment(sketch, "E691.left", {"start": v(534.1, -78.25) * mm, "end": v(534.1, -68.25) * mm});
            skLineSegment(sketch, "E691.right", {"start": v(537.1, -78.25) * mm, "end": v(537.1, -68.25) * mm});
            skPoint(sketch, "E691.middle", {"position": v(535.6, -73.25) * mm});
            skLineSegment(sketch, "E692.bottom", {"start": v(534.1, -138.25) * mm, "end": v(537.1, -138.25) * mm});
            skLineSegment(sketch, "E692.top", {"start": v(534.1, -128.25) * mm, "end": v(537.1, -128.25) * mm});
            skLineSegment(sketch, "E692.left", {"start": v(534.1, -138.25) * mm, "end": v(534.1, -128.25) * mm});
            skLineSegment(sketch, "E692.right", {"start": v(537.1, -138.25) * mm, "end": v(537.1, -128.25) * mm});
            skPoint(sketch, "E692.middle", {"position": v(535.6, -133.25) * mm});
            skLineSegment(sketch, "E693.bottom", {"start": v(534.1, -201.25) * mm, "end": v(537.1, -201.25) * mm});
            skLineSegment(sketch, "E693.top", {"start": v(534.1, -188.25) * mm, "end": v(537.1, -188.25) * mm});
            skLineSegment(sketch, "E693.left", {"start": v(534.1, -201.25) * mm, "end": v(534.1, -188.25) * mm});
            skLineSegment(sketch, "E693.right", {"start": v(537.1, -201.25) * mm, "end": v(537.1, -188.25) * mm});
            skPoint(sketch, "E693.middle", {"position": v(535.6, -194.75) * mm});
            skCircle(sketch, "E694", {"center": v(250, -295.4) * mm, "radius": 1.5 * mm});
            skCircle(sketch, "E695", {"center": v(149, -295.4) * mm, "radius": 1.5 * mm});
            skCircle(sketch, "E696", {"center": v(47, -295.4) * mm, "radius": 1.5 * mm});
            skCircle(sketch, "E697", {"center": v(-54, -295.4) * mm, "radius": 1.5 * mm});
            skLineSegment(sketch, "E698.bottom", {"start": v(-97.5, -292.9) * mm, "end": v(-79, -292.9) * mm});
            skLineSegment(sketch, "E698.top", {"start": v(-97.5, -297.9) * mm, "end": v(-79, -297.9) * mm});
            skLineSegment(sketch, "E698.left", {"start": v(-97.5, -292.9) * mm, "end": v(-97.5, -297.9) * mm});
            skLineSegment(sketch, "E698.right", {"start": v(-79, -292.9) * mm, "end": v(-79, -297.9) * mm});
            skPoint(sketch, "E698.middle", {"position": v(-88.25, -295.4) * mm});
            skLineSegment(sketch, "E699.bottom", {"start": v(-29, -292.9) * mm, "end": v(-19, -292.9) * mm});
            skLineSegment(sketch, "E699.top", {"start": v(-29, -297.9) * mm, "end": v(-19, -297.9) * mm});
            skLineSegment(sketch, "E699.left", {"start": v(-29, -292.9) * mm, "end": v(-29, -297.9) * mm});
            skLineSegment(sketch, "E699.right", {"start": v(-19, -292.9) * mm, "end": v(-19, -297.9) * mm});
            skPoint(sketch, "E699.middle", {"position": v(-24, -295.4) * mm});
            skLineSegment(sketch, "E700.bottom", {"start": v(275, -292.9) * mm, "end": v(293.5, -292.9) * mm});
            skLineSegment(sketch, "E700.top", {"start": v(275, -297.9) * mm, "end": v(293.5, -297.9) * mm});
            skLineSegment(sketch, "E700.left", {"start": v(275, -292.9) * mm, "end": v(275, -297.9) * mm});
            skLineSegment(sketch, "E700.right", {"start": v(293.5, -292.9) * mm, "end": v(293.5, -297.9) * mm});
            skPoint(sketch, "E700.middle", {"position": v(284.25, -295.4) * mm});
            skLineSegment(sketch, "E701.bottom", {"start": v(155, -292.9) * mm, "end": v(165, -292.9) * mm});
            skLineSegment(sketch, "E701.top", {"start": v(155, -297.9) * mm, "end": v(165, -297.9) * mm});
            skLineSegment(sketch, "E701.left", {"start": v(155, -292.9) * mm, "end": v(155, -297.9) * mm});
            skLineSegment(sketch, "E701.right", {"start": v(165, -292.9) * mm, "end": v(165, -297.9) * mm});
            skPoint(sketch, "E701.middle", {"position": v(160, -295.4) * mm});
            skLineSegment(sketch, "E702.bottom", {"start": v(215, -292.9) * mm, "end": v(225, -292.9) * mm});
            skLineSegment(sketch, "E702.top", {"start": v(215, -297.9) * mm, "end": v(225, -297.9) * mm});
            skLineSegment(sketch, "E702.left", {"start": v(215, -292.9) * mm, "end": v(215, -297.9) * mm});
            skLineSegment(sketch, "E702.right", {"start": v(225, -292.9) * mm, "end": v(225, -297.9) * mm});
            skPoint(sketch, "E702.middle", {"position": v(220, -295.4) * mm});
            skLineSegment(sketch, "E703.bottom", {"start": v(93, -292.9) * mm, "end": v(103, -292.9) * mm});
            skLineSegment(sketch, "E703.top", {"start": v(93, -297.9) * mm, "end": v(103, -297.9) * mm});
            skLineSegment(sketch, "E703.left", {"start": v(93, -292.9) * mm, "end": v(93, -297.9) * mm});
            skLineSegment(sketch, "E703.right", {"start": v(103, -292.9) * mm, "end": v(103, -297.9) * mm});
            skPoint(sketch, "E703.middle", {"position": v(98, -295.4) * mm});
            skLineSegment(sketch, "E704.bottom", {"start": v(31, -292.9) * mm, "end": v(41, -292.9) * mm});
            skLineSegment(sketch, "E704.top", {"start": v(31, -297.9) * mm, "end": v(41, -297.9) * mm});
            skLineSegment(sketch, "E704.left", {"start": v(31, -292.9) * mm, "end": v(31, -297.9) * mm});
            skLineSegment(sketch, "E704.right", {"start": v(41, -292.9) * mm, "end": v(41, -297.9) * mm});
            skPoint(sketch, "E704.middle", {"position": v(36, -295.4) * mm});
            skCircle(sketch, "E705", {"center": v(250, -383.77) * mm, "radius": 1.5 * mm});
            skCircle(sketch, "E706", {"center": v(149, -383.77) * mm, "radius": 1.5 * mm});
            skCircle(sketch, "E707", {"center": v(47, -383.77) * mm, "radius": 1.5 * mm});
            skCircle(sketch, "E708", {"center": v(-54, -383.77) * mm, "radius": 1.5 * mm});
            skLineSegment(sketch, "E709.bottom", {"start": v(-97.5, -382.27) * mm, "end": v(-79, -382.27) * mm});
            skLineSegment(sketch, "E709.top", {"start": v(-97.5, -385.27) * mm, "end": v(-79, -385.27) * mm});
            skLineSegment(sketch, "E709.left", {"start": v(-97.5, -382.27) * mm, "end": v(-97.5, -385.27) * mm});
            skLineSegment(sketch, "E709.right", {"start": v(-79, -382.27) * mm, "end": v(-79, -385.27) * mm});
            skPoint(sketch, "E709.middle", {"position": v(-88.25, -383.77) * mm});
            skLineSegment(sketch, "E710.bottom", {"start": v(-29, -382.27) * mm, "end": v(-19, -382.27) * mm});
            skLineSegment(sketch, "E710.top", {"start": v(-29, -385.27) * mm, "end": v(-19, -385.27) * mm});
            skLineSegment(sketch, "E710.left", {"start": v(-29, -382.27) * mm, "end": v(-29, -385.27) * mm});
            skLineSegment(sketch, "E710.right", {"start": v(-19, -382.27) * mm, "end": v(-19, -385.27) * mm});
            skPoint(sketch, "E710.middle", {"position": v(-24, -383.77) * mm});
            skLineSegment(sketch, "E711.bottom", {"start": v(275, -382.27) * mm, "end": v(293.5, -382.27) * mm});
            skLineSegment(sketch, "E711.top", {"start": v(275, -385.27) * mm, "end": v(293.5, -385.27) * mm});
            skLineSegment(sketch, "E711.left", {"start": v(275, -382.27) * mm, "end": v(275, -385.27) * mm});
            skLineSegment(sketch, "E711.right", {"start": v(293.5, -382.27) * mm, "end": v(293.5, -385.27) * mm});
            skPoint(sketch, "E711.middle", {"position": v(284.25, -383.77) * mm});
            skLineSegment(sketch, "E712.bottom", {"start": v(155, -382.27) * mm, "end": v(165, -382.27) * mm});
            skLineSegment(sketch, "E712.top", {"start": v(155, -385.27) * mm, "end": v(165, -385.27) * mm});
            skLineSegment(sketch, "E712.left", {"start": v(155, -382.27) * mm, "end": v(155, -385.27) * mm});
            skLineSegment(sketch, "E712.right", {"start": v(165, -382.27) * mm, "end": v(165, -385.27) * mm});
            skPoint(sketch, "E712.middle", {"position": v(160, -383.77) * mm});
            skLineSegment(sketch, "E713.bottom", {"start": v(215, -382.27) * mm, "end": v(225, -382.27) * mm});
            skLineSegment(sketch, "E713.top", {"start": v(215, -385.27) * mm, "end": v(225, -385.27) * mm});
            skLineSegment(sketch, "E713.left", {"start": v(215, -382.27) * mm, "end": v(215, -385.27) * mm});
            skLineSegment(sketch, "E713.right", {"start": v(225, -382.27) * mm, "end": v(225, -385.27) * mm});
            skPoint(sketch, "E713.middle", {"position": v(220, -383.77) * mm});
            skLineSegment(sketch, "E714.bottom", {"start": v(93, -382.27) * mm, "end": v(103, -382.27) * mm});
            skLineSegment(sketch, "E714.top", {"start": v(93, -385.27) * mm, "end": v(103, -385.27) * mm});
            skLineSegment(sketch, "E714.left", {"start": v(93, -382.27) * mm, "end": v(93, -385.27) * mm});
            skLineSegment(sketch, "E714.right", {"start": v(103, -382.27) * mm, "end": v(103, -385.27) * mm});
            skPoint(sketch, "E714.middle", {"position": v(98, -383.77) * mm});
            skLineSegment(sketch, "E715.bottom", {"start": v(31, -382.27) * mm, "end": v(41, -382.27) * mm});
            skLineSegment(sketch, "E715.top", {"start": v(31, -385.27) * mm, "end": v(41, -385.27) * mm});
            skLineSegment(sketch, "E715.left", {"start": v(31, -382.27) * mm, "end": v(31, -385.27) * mm});
            skLineSegment(sketch, "E715.right", {"start": v(41, -382.27) * mm, "end": v(41, -385.27) * mm});
            skPoint(sketch, "E715.middle", {"position": v(36, -383.77) * mm});
            skLineSegment(sketch, "E716", {"start": v(-100.5, -431.27) * mm, "end": v(-100.5, -379.27) * mm});
            skLineSegment(sketch, "E717", {"start": v(-100.5, -379.27) * mm, "end": v(296.5, -379.27) * mm});
            skLineSegment(sketch, "E718", {"start": v(296.5, -379.27) * mm, "end": v(296.5, -431.27) * mm});
            skLineSegment(sketch, "E719", {"start": v(296.5, -431.27) * mm, "end": v(-100.5, -431.27) * mm});
            skLineSegment(sketch, "E720", {"start": v(296.5, -329.9) * mm, "end": v(296.5, -289.9) * mm});
            skLineSegment(sketch, "E721", {"start": v(296.5, -289.9) * mm, "end": v(-100.5, -289.9) * mm});
            skLineSegment(sketch, "E722", {"start": v(-100.5, -289.9) * mm, "end": v(-100.5, -329.9) * mm});
            skLineSegment(sketch, "E723", {"start": v(-100.5, -329.9) * mm, "end": v(296.5, -329.9) * mm});
            skLineSegment(sketch, "E724", {"start": v(378.33, -204.25) * mm, "end": v(418.33, -204.25) * mm});
            skLineSegment(sketch, "E725", {"start": v(418.33, -204.25) * mm, "end": v(418.33, 204.25) * mm});
            skLineSegment(sketch, "E726", {"start": v(418.33, 204.25) * mm, "end": v(378.33, 204.25) * mm});
            skLineSegment(sketch, "E727", {"start": v(378.33, 204.25) * mm, "end": v(378.33, -204.25) * mm});
            skLineSegment(sketch, "E728", {"start": v(488.1, -204.25) * mm, "end": v(540.1, -204.25) * mm});
            skLineSegment(sketch, "E729", {"start": v(540.1, -204.25) * mm, "end": v(540.1, 204.25) * mm});
            skLineSegment(sketch, "E730", {"start": v(540.1, 204.25) * mm, "end": v(488.1, 204.25) * mm});
            skLineSegment(sketch, "E731", {"start": v(488.1, 204.25) * mm, "end": v(488.1, -204.25) * mm});
            skCircle(sketch, "E732", {"center": v(-90.5, -426.27) * mm, "radius": 1.5 * mm});
            skCircle(sketch, "E733", {"center": v(-90.5, -401.27) * mm, "radius": 1.5 * mm});
            skCircle(sketch, "E734", {"center": v(286.5, -401.27) * mm, "radius": 1.5 * mm});
            skCircle(sketch, "E735", {"center": v(286.5, -426.27) * mm, "radius": 1.5 * mm});
            skCircle(sketch, "E736", {"center": v(286.5, -304.9) * mm, "radius": 1.5 * mm});
            skCircle(sketch, "E737", {"center": v(286.5, -319.9) * mm, "radius": 1.5 * mm});
            skCircle(sketch, "E738", {"center": v(-90.5, -304.9) * mm, "radius": 1.5 * mm});
            skCircle(sketch, "E739", {"center": v(-90.5, -319.9) * mm, "radius": 1.5 * mm});
            skCircle(sketch, "E740", {"center": v(383.33, -194.25) * mm, "radius": 1.5 * mm});
            skCircle(sketch, "E741", {"center": v(398.33, -194.25) * mm, "radius": 1.5 * mm});
            skCircle(sketch, "E742", {"center": v(498.1, -194.25) * mm, "radius": 1.5 * mm});
            skCircle(sketch, "E743", {"center": v(528.1, -194.25) * mm, "radius": 1.5 * mm});
            skLineSegment(sketch, "E744", {"start": v(378.33, 217.25) * mm, "end": v(378.33, 204.25) * mm});
            skLineSegment(sketch, "E745", {"start": v(488.1, 204.25) * mm, "end": v(488.1, 217.25) * mm});
            skLineSegment(sketch, "E746", {"start": v(488.1, 217.25) * mm, "end": v(540.1, 217.25) * mm});
            skLineSegment(sketch, "E747", {"start": v(540.1, 217.25) * mm, "end": v(540.1, 204.25) * mm});
            skLineSegment(sketch, "E748", {"start": v(378.33, 217.25) * mm, "end": v(418.33, 217.25) * mm});
            skLineSegment(sketch, "E749", {"start": v(418.33, 217.25) * mm, "end": v(418.33, 204.25) * mm});
            skLineSegment(sketch, "E750.bottom", {"start": v(393.33, 214.25) * mm, "end": v(403.33, 214.25) * mm});
            skLineSegment(sketch, "E750.top", {"start": v(393.33, 211.25) * mm, "end": v(403.33, 211.25) * mm});
            skLineSegment(sketch, "E750.left", {"start": v(393.33, 214.25) * mm, "end": v(393.33, 211.25) * mm});
            skLineSegment(sketch, "E750.right", {"start": v(403.33, 214.25) * mm, "end": v(403.33, 211.25) * mm});
            skPoint(sketch, "E751.middle", {"position": v(398.33, 212.75) * mm});
            skPoint(sketch, "E751.middle.positionSnap0", {"position": v(398.33, 211.25) * mm});
            skPoint(sketch, "E751.middle.positionSnap1", {"position": v(393.33, 212.75) * mm});
            skPoint(sketch, "E751.centerSnap0", {"position": v(398.33, 211.25) * mm});
            skPoint(sketch, "E751.centerSnap1", {"position": v(393.33, 212.75) * mm});
            skCircle(sketch, "E752", {"center": v(388.33, 212.75) * mm, "radius": 1.5 * mm});
            skLineSegment(sketch, "E753.bottom", {"start": v(501.1, 211.25) * mm, "end": v(491.1, 211.25) * mm});
            skLineSegment(sketch, "E753.top", {"start": v(501.1, 214.25) * mm, "end": v(491.1, 214.25) * mm});
            skLineSegment(sketch, "E753.left", {"start": v(501.1, 211.25) * mm, "end": v(501.1, 214.25) * mm});
            skLineSegment(sketch, "E753.right", {"start": v(491.1, 211.25) * mm, "end": v(491.1, 214.25) * mm});
            skPoint(sketch, "E753.middle", {"position": v(496.1, 212.75) * mm});
            skCircle(sketch, "E754", {"center": v(508.6, 212.75) * mm, "radius": 1.5 * mm});
            skLineSegment(sketch, "E755.bottom", {"start": v(516.1, 214.25) * mm, "end": v(526.1, 214.25) * mm});
            skLineSegment(sketch, "E755.top", {"start": v(516.1, 211.25) * mm, "end": v(526.1, 211.25) * mm});
            skLineSegment(sketch, "E755.left", {"start": v(516.1, 214.25) * mm, "end": v(516.1, 211.25) * mm});
            skLineSegment(sketch, "E755.right", {"start": v(526.1, 214.25) * mm, "end": v(526.1, 211.25) * mm});
            skPoint(sketch, "E755.middle", {"position": v(521.1, 212.75) * mm});
            skCircle(sketch, "E756", {"center": v(152, 486.03) * mm, "radius": 1.5 * mm});
            skCircle(sketch, "E757", {"center": v(51, 486.03) * mm, "radius": 1.5 * mm});
            skCircle(sketch, "E758", {"center": v(-51, 486.03) * mm, "radius": 1.5 * mm});
            skCircle(sketch, "E759", {"center": v(-152, 486.03) * mm, "radius": 1.5 * mm});
            skLineSegment(sketch, "E760.bottom", {"start": v(-195.5, 488.53) * mm, "end": v(-177, 488.53) * mm});
            skLineSegment(sketch, "E760.top", {"start": v(-195.5, 483.53) * mm, "end": v(-177, 483.53) * mm});
            skLineSegment(sketch, "E760.left", {"start": v(-195.5, 488.53) * mm, "end": v(-195.5, 483.53) * mm});
            skLineSegment(sketch, "E760.right", {"start": v(-177, 488.53) * mm, "end": v(-177, 483.53) * mm});
            skPoint(sketch, "E760.middle", {"position": v(-186.25, 486.03) * mm});
            skLineSegment(sketch, "E761.bottom", {"start": v(-127, 488.53) * mm, "end": v(-117, 488.53) * mm});
            skLineSegment(sketch, "E761.top", {"start": v(-127, 483.53) * mm, "end": v(-117, 483.53) * mm});
            skLineSegment(sketch, "E761.left", {"start": v(-127, 488.53) * mm, "end": v(-127, 483.53) * mm});
            skLineSegment(sketch, "E761.right", {"start": v(-117, 488.53) * mm, "end": v(-117, 483.53) * mm});
            skPoint(sketch, "E761.middle", {"position": v(-122, 486.03) * mm});
            skLineSegment(sketch, "E762.bottom", {"start": v(177, 488.53) * mm, "end": v(195.5, 488.53) * mm});
            skLineSegment(sketch, "E762.top", {"start": v(177, 483.53) * mm, "end": v(195.5, 483.53) * mm});
            skLineSegment(sketch, "E762.left", {"start": v(177, 488.53) * mm, "end": v(177, 483.53) * mm});
            skLineSegment(sketch, "E762.right", {"start": v(195.5, 488.53) * mm, "end": v(195.5, 483.53) * mm});
            skPoint(sketch, "E762.middle", {"position": v(186.25, 486.03) * mm});
            skLineSegment(sketch, "E763.bottom", {"start": v(57, 488.53) * mm, "end": v(67, 488.53) * mm});
            skLineSegment(sketch, "E763.top", {"start": v(57, 483.53) * mm, "end": v(67, 483.53) * mm});
            skLineSegment(sketch, "E763.left", {"start": v(57, 488.53) * mm, "end": v(57, 483.53) * mm});
            skLineSegment(sketch, "E763.right", {"start": v(67, 488.53) * mm, "end": v(67, 483.53) * mm});
            skPoint(sketch, "E763.middle", {"position": v(62, 486.03) * mm});
            skLineSegment(sketch, "E764.bottom", {"start": v(117, 488.53) * mm, "end": v(127, 488.53) * mm});
            skLineSegment(sketch, "E764.top", {"start": v(117, 483.53) * mm, "end": v(127, 483.53) * mm});
            skLineSegment(sketch, "E764.left", {"start": v(117, 488.53) * mm, "end": v(117, 483.53) * mm});
            skLineSegment(sketch, "E764.right", {"start": v(127, 488.53) * mm, "end": v(127, 483.53) * mm});
            skPoint(sketch, "E764.middle", {"position": v(122, 486.03) * mm});
            skLineSegment(sketch, "E765.bottom", {"start": v(-5, 488.53) * mm, "end": v(5, 488.53) * mm});
            skLineSegment(sketch, "E765.top", {"start": v(-5, 483.53) * mm, "end": v(5, 483.53) * mm});
            skLineSegment(sketch, "E765.left", {"start": v(-5, 488.53) * mm, "end": v(-5, 483.53) * mm});
            skLineSegment(sketch, "E765.right", {"start": v(5, 488.53) * mm, "end": v(5, 483.53) * mm});
            skPoint(sketch, "E765.middle", {"position": v(0, 486.03) * mm});
            skLineSegment(sketch, "E766.bottom", {"start": v(-67, 488.53) * mm, "end": v(-57, 488.53) * mm});
            skLineSegment(sketch, "E766.top", {"start": v(-67, 483.53) * mm, "end": v(-57, 483.53) * mm});
            skLineSegment(sketch, "E766.left", {"start": v(-67, 488.53) * mm, "end": v(-67, 483.53) * mm});
            skLineSegment(sketch, "E766.right", {"start": v(-57, 488.53) * mm, "end": v(-57, 483.53) * mm});
            skPoint(sketch, "E766.middle", {"position": v(-62, 486.03) * mm});
            skCircle(sketch, "E767", {"center": v(152, 397.66) * mm, "radius": 1.5 * mm});
            skCircle(sketch, "E768", {"center": v(51, 397.66) * mm, "radius": 1.5 * mm});
            skCircle(sketch, "E769", {"center": v(-51, 397.66) * mm, "radius": 1.5 * mm});
            skCircle(sketch, "E770", {"center": v(-152, 397.66) * mm, "radius": 1.5 * mm});
            skLineSegment(sketch, "E771.bottom", {"start": v(-195.5, 399.16) * mm, "end": v(-177, 399.16) * mm});
            skLineSegment(sketch, "E771.top", {"start": v(-195.5, 396.16) * mm, "end": v(-177, 396.16) * mm});
            skLineSegment(sketch, "E771.left", {"start": v(-195.5, 399.16) * mm, "end": v(-195.5, 396.16) * mm});
            skLineSegment(sketch, "E771.right", {"start": v(-177, 399.16) * mm, "end": v(-177, 396.16) * mm});
            skPoint(sketch, "E771.middle", {"position": v(-186.25, 397.66) * mm});
            skLineSegment(sketch, "E772.bottom", {"start": v(-127, 399.16) * mm, "end": v(-117, 399.16) * mm});
            skLineSegment(sketch, "E772.top", {"start": v(-127, 396.16) * mm, "end": v(-117, 396.16) * mm});
            skLineSegment(sketch, "E772.left", {"start": v(-127, 399.16) * mm, "end": v(-127, 396.16) * mm});
            skLineSegment(sketch, "E772.right", {"start": v(-117, 399.16) * mm, "end": v(-117, 396.16) * mm});
            skPoint(sketch, "E772.middle", {"position": v(-122, 397.66) * mm});
            skLineSegment(sketch, "E773.bottom", {"start": v(177, 399.16) * mm, "end": v(195.5, 399.16) * mm});
            skLineSegment(sketch, "E773.top", {"start": v(177, 396.16) * mm, "end": v(195.5, 396.16) * mm});
            skLineSegment(sketch, "E773.left", {"start": v(177, 399.16) * mm, "end": v(177, 396.16) * mm});
            skLineSegment(sketch, "E773.right", {"start": v(195.5, 399.16) * mm, "end": v(195.5, 396.16) * mm});
            skPoint(sketch, "E773.middle", {"position": v(186.25, 397.66) * mm});
            skLineSegment(sketch, "E774.bottom", {"start": v(57, 399.16) * mm, "end": v(67, 399.16) * mm});
            skLineSegment(sketch, "E774.top", {"start": v(57, 396.16) * mm, "end": v(67, 396.16) * mm});
            skLineSegment(sketch, "E774.left", {"start": v(57, 399.16) * mm, "end": v(57, 396.16) * mm});
            skLineSegment(sketch, "E774.right", {"start": v(67, 399.16) * mm, "end": v(67, 396.16) * mm});
            skPoint(sketch, "E774.middle", {"position": v(62, 397.66) * mm});
            skLineSegment(sketch, "E775.bottom", {"start": v(117, 399.16) * mm, "end": v(127, 399.16) * mm});
            skLineSegment(sketch, "E775.top", {"start": v(117, 396.16) * mm, "end": v(127, 396.16) * mm});
            skLineSegment(sketch, "E775.left", {"start": v(117, 399.16) * mm, "end": v(117, 396.16) * mm});
            skLineSegment(sketch, "E775.right", {"start": v(127, 399.16) * mm, "end": v(127, 396.16) * mm});
            skPoint(sketch, "E775.middle", {"position": v(122, 397.66) * mm});
            skLineSegment(sketch, "E776.bottom", {"start": v(-5, 399.16) * mm, "end": v(5, 399.16) * mm});
            skLineSegment(sketch, "E776.top", {"start": v(-5, 396.16) * mm, "end": v(5, 396.16) * mm});
            skLineSegment(sketch, "E776.left", {"start": v(-5, 399.16) * mm, "end": v(-5, 396.16) * mm});
            skLineSegment(sketch, "E776.right", {"start": v(5, 399.16) * mm, "end": v(5, 396.16) * mm});
            skPoint(sketch, "E776.middle", {"position": v(0, 397.66) * mm});
            skLineSegment(sketch, "E777.bottom", {"start": v(-67, 399.16) * mm, "end": v(-57, 399.16) * mm});
            skLineSegment(sketch, "E777.top", {"start": v(-67, 396.16) * mm, "end": v(-57, 396.16) * mm});
            skLineSegment(sketch, "E777.left", {"start": v(-67, 399.16) * mm, "end": v(-67, 396.16) * mm});
            skLineSegment(sketch, "E777.right", {"start": v(-57, 399.16) * mm, "end": v(-57, 396.16) * mm});
            skPoint(sketch, "E777.middle", {"position": v(-62, 397.66) * mm});
            skLineSegment(sketch, "E778", {"start": v(-198.5, 350.16) * mm, "end": v(-198.5, 402.16) * mm});
            skLineSegment(sketch, "E779", {"start": v(-198.5, 402.16) * mm, "end": v(198.5, 402.16) * mm});
            skLineSegment(sketch, "E780", {"start": v(198.5, 402.16) * mm, "end": v(198.5, 350.16) * mm});
            skLineSegment(sketch, "E781", {"start": v(198.5, 350.16) * mm, "end": v(-198.5, 350.16) * mm});
            skLineSegment(sketch, "E782", {"start": v(198.5, 451.53) * mm, "end": v(198.5, 491.53) * mm});
            skLineSegment(sketch, "E783", {"start": v(198.5, 491.53) * mm, "end": v(-198.5, 491.53) * mm});
            skLineSegment(sketch, "E784", {"start": v(-198.5, 491.53) * mm, "end": v(-198.5, 451.53) * mm});
            skLineSegment(sketch, "E785", {"start": v(-198.5, 451.53) * mm, "end": v(198.5, 451.53) * mm});
            skLineSegment(sketch, "E786.bottom", {"start": v(198.5, 350.16) * mm, "end": v(205.5, 350.16) * mm});
            skLineSegment(sketch, "E786.top", {"start": v(198.5, 402.16) * mm, "end": v(205.5, 402.16) * mm});
            skLineSegment(sketch, "E786.left", {"start": v(198.5, 350.16) * mm, "end": v(198.5, 402.16) * mm});
            skLineSegment(sketch, "E786.right", {"start": v(205.5, 350.16) * mm, "end": v(205.5, 402.16) * mm});
            skLineSegment(sketch, "E787.bottom", {"start": v(198.5, 491.53) * mm, "end": v(205.5, 491.53) * mm});
            skLineSegment(sketch, "E787.top", {"start": v(198.5, 451.53) * mm, "end": v(205.5, 451.53) * mm});
            skLineSegment(sketch, "E787.left", {"start": v(198.5, 491.53) * mm, "end": v(198.5, 451.53) * mm});
            skLineSegment(sketch, "E787.right", {"start": v(205.5, 491.53) * mm, "end": v(205.5, 451.53) * mm});
            skLineSegment(sketch, "E788", {"start": v(-205.5, 402.16) * mm, "end": v(-205.5, 350.16) * mm});
            skLineSegment(sketch, "E789.bottom", {"start": v(-205.5, 350.16) * mm, "end": v(-198.5, 350.16) * mm});
            skLineSegment(sketch, "E790.bottom", {"start": v(-205.5, 491.53) * mm, "end": v(-198.5, 491.53) * mm});
            skLineSegment(sketch, "E790.top", {"start": v(-205.5, 451.53) * mm, "end": v(-198.5, 451.53) * mm});
            skLineSegment(sketch, "E790.left", {"start": v(-205.5, 491.53) * mm, "end": v(-205.5, 451.53) * mm});
            skLineSegment(sketch, "E791", {"start": v(-205.5, 402.16) * mm, "end": v(-198.5, 402.16) * mm});
            skLineSegment(sketch, "E792", {"start": v(199.1, 459.83) * mm, "end": v(205.5, 459.83) * mm});
            skLineSegment(sketch, "E793", {"start": v(199.1, 458.33) * mm, "end": v(199.1, 459.83) * mm});
            skLineSegment(sketch, "E794", {"start": v(196.5, 458.33) * mm, "end": v(199.1, 458.33) * mm});
            skLineSegment(sketch, "E795", {"start": v(196.5, 459.83) * mm, "end": v(196.5, 458.33) * mm});
            skLineSegment(sketch, "E796", {"start": v(191.5, 459.83) * mm, "end": v(196.5, 459.83) * mm});
            skLineSegment(sketch, "E797", {"start": v(191.5, 463.23) * mm, "end": v(191.5, 459.83) * mm});
            skLineSegment(sketch, "E798", {"start": v(196.5, 463.23) * mm, "end": v(191.5, 463.23) * mm});
            skLineSegment(sketch, "E799", {"start": v(196.5, 464.73) * mm, "end": v(196.5, 463.23) * mm});
            skLineSegment(sketch, "E800", {"start": v(199.1, 464.73) * mm, "end": v(196.5, 464.73) * mm});
            skLineSegment(sketch, "E801", {"start": v(199.1, 463.23) * mm, "end": v(199.1, 464.73) * mm});
            skLineSegment(sketch, "E802", {"start": v(205.5, 463.23) * mm, "end": v(199.1, 463.23) * mm});
            skLineSegment(sketch, "E803", {"start": v(-199.1, 463.23) * mm, "end": v(-205.5, 463.23) * mm});
            skLineSegment(sketch, "E804", {"start": v(-199.1, 464.73) * mm, "end": v(-199.1, 463.23) * mm});
            skLineSegment(sketch, "E805", {"start": v(-196.5, 464.73) * mm, "end": v(-199.1, 464.73) * mm});
            skLineSegment(sketch, "E806", {"start": v(-196.5, 463.23) * mm, "end": v(-196.5, 464.73) * mm});
            skLineSegment(sketch, "E807", {"start": v(-191.5, 463.23) * mm, "end": v(-196.5, 463.23) * mm});
            skLineSegment(sketch, "E808", {"start": v(-191.5, 459.83) * mm, "end": v(-191.5, 463.23) * mm});
            skLineSegment(sketch, "E809", {"start": v(-196.5, 459.83) * mm, "end": v(-191.5, 459.83) * mm});
            skLineSegment(sketch, "E810", {"start": v(-196.5, 458.33) * mm, "end": v(-196.5, 459.83) * mm});
            skLineSegment(sketch, "E811", {"start": v(-199.1, 458.33) * mm, "end": v(-196.5, 458.33) * mm});
            skLineSegment(sketch, "E812", {"start": v(-199.1, 459.83) * mm, "end": v(-199.1, 458.33) * mm});
            skLineSegment(sketch, "E813", {"start": v(-205.5, 459.83) * mm, "end": v(-199.1, 459.83) * mm});
            skLineSegment(sketch, "E814.bottom", {"start": v(-205.5, 466.53) * mm, "end": v(-208.5, 466.53) * mm});
            skLineSegment(sketch, "E814.top", {"start": v(-205.5, 476.53) * mm, "end": v(-208.5, 476.53) * mm});
            skLineSegment(sketch, "E814.left", {"start": v(-205.5, 466.53) * mm, "end": v(-205.5, 476.53) * mm});
            skLineSegment(sketch, "E814.right", {"start": v(-208.5, 466.53) * mm, "end": v(-208.5, 476.53) * mm});
            skLineSegment(sketch, "E815.bottom", {"start": v(205.5, 466.53) * mm, "end": v(208.5, 466.53) * mm});
            skLineSegment(sketch, "E815.top", {"start": v(205.5, 476.53) * mm, "end": v(208.5, 476.53) * mm});
            skLineSegment(sketch, "E815.left", {"start": v(205.5, 466.53) * mm, "end": v(205.5, 476.53) * mm});
            skLineSegment(sketch, "E815.right", {"start": v(208.5, 466.53) * mm, "end": v(208.5, 476.53) * mm});
            skLineSegment(sketch, "E816.bottom", {"start": v(205.5, 353.16) * mm, "end": v(208.5, 353.16) * mm});
            skLineSegment(sketch, "E816.top", {"start": v(205.5, 363.16) * mm, "end": v(208.5, 363.16) * mm});
            skLineSegment(sketch, "E816.left", {"start": v(205.5, 353.16) * mm, "end": v(205.5, 363.16) * mm});
            skLineSegment(sketch, "E816.right", {"start": v(208.5, 353.16) * mm, "end": v(208.5, 363.16) * mm});
            skLineSegment(sketch, "E817", {"start": v(199.1, 368.96) * mm, "end": v(205.5, 368.96) * mm});
            skLineSegment(sketch, "E818", {"start": v(199.1, 367.46) * mm, "end": v(199.1, 368.96) * mm});
            skLineSegment(sketch, "E819", {"start": v(196.5, 367.46) * mm, "end": v(199.1, 367.46) * mm});
            skLineSegment(sketch, "E820", {"start": v(196.5, 368.96) * mm, "end": v(196.5, 367.46) * mm});
            skLineSegment(sketch, "E821", {"start": v(191.5, 368.96) * mm, "end": v(196.5, 368.96) * mm});
            skLineSegment(sketch, "E822", {"start": v(191.5, 372.36) * mm, "end": v(191.5, 368.96) * mm});
            skLineSegment(sketch, "E823", {"start": v(196.5, 372.36) * mm, "end": v(191.5, 372.36) * mm});
            skLineSegment(sketch, "E824", {"start": v(196.5, 373.86) * mm, "end": v(196.5, 372.36) * mm});
            skLineSegment(sketch, "E825", {"start": v(199.1, 373.86) * mm, "end": v(196.5, 373.86) * mm});
            skLineSegment(sketch, "E826", {"start": v(199.1, 372.36) * mm, "end": v(199.1, 373.86) * mm});
            skLineSegment(sketch, "E827", {"start": v(205.5, 372.36) * mm, "end": v(199.1, 372.36) * mm});
            skLineSegment(sketch, "E828.bottom", {"start": v(205.5, 378.16) * mm, "end": v(208.5, 378.16) * mm});
            skLineSegment(sketch, "E828.top", {"start": v(205.5, 388.16) * mm, "end": v(208.5, 388.16) * mm});
            skLineSegment(sketch, "E828.left", {"start": v(205.5, 378.16) * mm, "end": v(205.5, 388.16) * mm});
            skLineSegment(sketch, "E828.right", {"start": v(208.5, 378.16) * mm, "end": v(208.5, 388.16) * mm});
            skLineSegment(sketch, "E829.bottom", {"start": v(-205.5, 353.16) * mm, "end": v(-208.5, 353.16) * mm});
            skLineSegment(sketch, "E829.top", {"start": v(-205.5, 363.16) * mm, "end": v(-208.5, 363.16) * mm});
            skLineSegment(sketch, "E829.left", {"start": v(-205.5, 353.16) * mm, "end": v(-205.5, 363.16) * mm});
            skLineSegment(sketch, "E829.right", {"start": v(-208.5, 353.16) * mm, "end": v(-208.5, 363.16) * mm});
            skLineSegment(sketch, "E830.bottom", {"start": v(-205.5, 378.16) * mm, "end": v(-208.5, 378.16) * mm});
            skLineSegment(sketch, "E830.top", {"start": v(-205.5, 388.16) * mm, "end": v(-208.5, 388.16) * mm});
            skLineSegment(sketch, "E830.left", {"start": v(-205.5, 378.16) * mm, "end": v(-205.5, 388.16) * mm});
            skLineSegment(sketch, "E830.right", {"start": v(-208.5, 378.16) * mm, "end": v(-208.5, 388.16) * mm});
            skLineSegment(sketch, "E831", {"start": v(-199.1, 372.36) * mm, "end": v(-205.5, 372.36) * mm});
            skLineSegment(sketch, "E832", {"start": v(-199.1, 373.86) * mm, "end": v(-199.1, 372.36) * mm});
            skLineSegment(sketch, "E833", {"start": v(-196.5, 373.86) * mm, "end": v(-199.1, 373.86) * mm});
            skLineSegment(sketch, "E834", {"start": v(-196.5, 372.36) * mm, "end": v(-196.5, 373.86) * mm});
            skLineSegment(sketch, "E835", {"start": v(-191.5, 372.36) * mm, "end": v(-196.5, 372.36) * mm});
            skLineSegment(sketch, "E836", {"start": v(-191.5, 368.96) * mm, "end": v(-191.5, 372.36) * mm});
            skLineSegment(sketch, "E837", {"start": v(-196.5, 368.96) * mm, "end": v(-191.5, 368.96) * mm});
            skLineSegment(sketch, "E838", {"start": v(-196.5, 367.46) * mm, "end": v(-196.5, 368.96) * mm});
            skLineSegment(sketch, "E839", {"start": v(-199.1, 367.46) * mm, "end": v(-196.5, 367.46) * mm});
            skLineSegment(sketch, "E840", {"start": v(-199.1, 368.96) * mm, "end": v(-199.1, 367.46) * mm});
            skLineSegment(sketch, "E841", {"start": v(-205.5, 368.96) * mm, "end": v(-199.1, 368.96) * mm});
            skCircle(sketch, "E842", {"center": v(-460.62, 303.71) * mm, "radius": 1.5 * mm});
            skCircle(sketch, "E843", {"center": v(-451.12, 303.71) * mm, "radius": 1.5 * mm});
            skPoint(sketch, "E844.middle", {"position": v(-455.87, 303.71) * mm});
            skLineSegment(sketch, "E845", {"start": v(-465.82, 302.19) * mm, "end": v(-445.82, 302.19) * mm});
            skLineSegment(sketch, "E846", {"start": v(-445.82, 302.19) * mm, "end": v(-445.82, 313.19) * mm});
            skLineSegment(sketch, "E847", {"start": v(-445.82, 313.19) * mm, "end": v(-465.82, 313.19) * mm});
            skLineSegment(sketch, "E848", {"start": v(-465.82, 313.19) * mm, "end": v(-465.82, 302.19) * mm});
            skLineSegment(sketch, "E849", {"start": v(-445.82, 313.19) * mm, "end": v(-463.16, 318) * mm});
            skLineSegment(sketch, "E850", {"start": v(-463.16, 318) * mm, "end": v(-449.82, 313.19) * mm});
            skLineSegment(sketch, "E851", {"start": v(398.33, -194.25) * mm, "end": v(398.33, -189.25) * mm});
            skCircle(sketch, "E852", {"center": v(388.83, -189.25) * mm, "radius": 1.5 * mm});
            skCircle(sketch, "E853", {"center": v(398.33, -189.25) * mm, "radius": 1.5 * mm});
            skCircle(sketch, "E854", {"center": v(388.83, -179.25) * mm, "radius": 1.5 * mm});
            skCircle(sketch, "E855", {"center": v(398.33, -179.25) * mm, "radius": 1.5 * mm});
            skLineSegment(sketch, "E856", {"start": v(390.33, -189.25) * mm, "end": v(390.33, -179.25) * mm});
            skLineSegment(sketch, "E857", {"start": v(387.33, -189.25) * mm, "end": v(387.33, -179.25) * mm});
            skLineSegment(sketch, "E858", {"start": v(396.83, -179.25) * mm, "end": v(396.83, -189.25) * mm});
            skLineSegment(sketch, "E859", {"start": v(399.83, -179.25) * mm, "end": v(399.83, -189.25) * mm});
            skLineSegment(sketch, "E860", {"start": v(388.83, -189.25) * mm, "end": v(388.83, 130.75) * mm});
            skCircle(sketch, "E861", {"center": v(388.83, 120.75) * mm, "radius": 1.5 * mm});
            skCircle(sketch, "E862", {"center": v(398.33, 120.75) * mm, "radius": 1.5 * mm});
            skCircle(sketch, "E863", {"center": v(388.83, 135.75) * mm, "radius": 1.5 * mm});
            skCircle(sketch, "E864", {"center": v(398.33, 135.75) * mm, "radius": 1.5 * mm});
            skLineSegment(sketch, "E865", {"start": v(293.5, 211.25) * mm, "end": v(303.5, 211.25) * mm});
            skLineSegment(sketch, "E866", {"start": v(303.5, 211.25) * mm, "end": v(303.5, 201.25) * mm});
            skLineSegment(sketch, "E867", {"start": v(-107.5, 201.25) * mm, "end": v(-107.5, 211.25) * mm});
            skLineSegment(sketch, "E868", {"start": v(-107.5, 211.25) * mm, "end": v(-97.5, 211.25) * mm});
            skLineSegment(sketch, "E869", {"start": v(387.33, 135.75) * mm, "end": v(387.33, 120.75) * mm});
            skLineSegment(sketch, "E870", {"start": v(390.33, 135.75) * mm, "end": v(390.33, 120.75) * mm});
            skLineSegment(sketch, "E871", {"start": v(396.83, 135.75) * mm, "end": v(396.83, 120.75) * mm});
            skLineSegment(sketch, "E872", {"start": v(399.83, 135.75) * mm, "end": v(399.83, 120.75) * mm});
            skCircle(sketch, "E873", {"center": v(-157, -56.75) * mm, "radius": 1.5 * mm});
            skCircle(sketch, "E874", {"center": v(-157, -177.75) * mm, "radius": 1.5 * mm});
            skCircle(sketch, "E875", {"center": v(-157, 35.25) * mm, "radius": 1.5 * mm});
            skCircle(sketch, "E876", {"center": v(-157, 126.25) * mm, "radius": 1.5 * mm});
            skLineSegment(sketch, "E877.bottom", {"start": v(-154.5, 181.25) * mm, "end": v(-159.5, 181.25) * mm});
            skLineSegment(sketch, "E877.top", {"start": v(-154.5, 201.25) * mm, "end": v(-159.5, 201.25) * mm});
            skLineSegment(sketch, "E877.left", {"start": v(-154.5, 181.25) * mm, "end": v(-154.5, 201.25) * mm});
            skLineSegment(sketch, "E877.right", {"start": v(-159.5, 181.25) * mm, "end": v(-159.5, 201.25) * mm});
            skPoint(sketch, "E877.middle", {"position": v(-157, 191.25) * mm});
            skLineSegment(sketch, "E878.bottom", {"start": v(-159.5, 105.75) * mm, "end": v(-154.5, 105.75) * mm});
            skLineSegment(sketch, "E878.top", {"start": v(-159.5, 115.75) * mm, "end": v(-154.5, 115.75) * mm});
            skLineSegment(sketch, "E878.left", {"start": v(-159.5, 105.75) * mm, "end": v(-159.5, 115.75) * mm});
            skLineSegment(sketch, "E878.right", {"start": v(-154.5, 105.75) * mm, "end": v(-154.5, 115.75) * mm});
            skPoint(sketch, "E878.middle", {"position": v(-157, 110.75) * mm});
            skLineSegment(sketch, "E879.bottom", {"start": v(-159.5, 45.75) * mm, "end": v(-154.5, 45.75) * mm});
            skLineSegment(sketch, "E879.top", {"start": v(-159.5, 55.75) * mm, "end": v(-154.5, 55.75) * mm});
            skLineSegment(sketch, "E879.left", {"start": v(-159.5, 45.75) * mm, "end": v(-159.5, 55.75) * mm});
            skLineSegment(sketch, "E879.right", {"start": v(-154.5, 45.75) * mm, "end": v(-154.5, 55.75) * mm});
            skPoint(sketch, "E879.middle", {"position": v(-157, 50.75) * mm});
            skLineSegment(sketch, "E880.bottom", {"start": v(-159.5, -16.25) * mm, "end": v(-154.5, -16.25) * mm});
            skLineSegment(sketch, "E880.top", {"start": v(-159.5, -6.25) * mm, "end": v(-154.5, -6.25) * mm});
            skLineSegment(sketch, "E880.left", {"start": v(-159.5, -16.25) * mm, "end": v(-159.5, -6.25) * mm});
            skLineSegment(sketch, "E880.right", {"start": v(-154.5, -16.25) * mm, "end": v(-154.5, -6.25) * mm});
            skPoint(sketch, "E880.middle", {"position": v(-157, -11.25) * mm});
            skLineSegment(sketch, "E881.bottom", {"start": v(-159.5, -78.25) * mm, "end": v(-154.5, -78.25) * mm});
            skLineSegment(sketch, "E881.top", {"start": v(-159.5, -68.25) * mm, "end": v(-154.5, -68.25) * mm});
            skLineSegment(sketch, "E881.left", {"start": v(-159.5, -78.25) * mm, "end": v(-159.5, -68.25) * mm});
            skLineSegment(sketch, "E881.right", {"start": v(-154.5, -78.25) * mm, "end": v(-154.5, -68.25) * mm});
            skPoint(sketch, "E881.middle", {"position": v(-157, -73.25) * mm});
            skLineSegment(sketch, "E882.bottom", {"start": v(-159.5, -138.25) * mm, "end": v(-154.5, -138.25) * mm});
            skLineSegment(sketch, "E882.top", {"start": v(-159.5, -128.25) * mm, "end": v(-154.5, -128.25) * mm});
            skLineSegment(sketch, "E882.left", {"start": v(-159.5, -138.25) * mm, "end": v(-159.5, -128.25) * mm});
            skLineSegment(sketch, "E882.right", {"start": v(-154.5, -138.25) * mm, "end": v(-154.5, -128.25) * mm});
            skPoint(sketch, "E882.middle", {"position": v(-157, -133.25) * mm});
            skLineSegment(sketch, "E883.bottom", {"start": v(-159.5, -201.25) * mm, "end": v(-154.5, -201.25) * mm});
            skLineSegment(sketch, "E883.top", {"start": v(-159.5, -188.25) * mm, "end": v(-154.5, -188.25) * mm});
            skLineSegment(sketch, "E883.left", {"start": v(-159.5, -201.25) * mm, "end": v(-159.5, -188.25) * mm});
            skLineSegment(sketch, "E883.right", {"start": v(-154.5, -201.25) * mm, "end": v(-154.5, -188.25) * mm});
            skPoint(sketch, "E883.middle", {"position": v(-157, -194.75) * mm});
            skLineSegment(sketch, "E884", {"start": v(-191.5, -204.25) * mm, "end": v(-151.5, -204.25) * mm});
            skLineSegment(sketch, "E885", {"start": v(-151.5, -204.25) * mm, "end": v(-151.5, 204.25) * mm});
            skLineSegment(sketch, "E886", {"start": v(-151.5, 204.25) * mm, "end": v(-191.5, 204.25) * mm});
            skLineSegment(sketch, "E887", {"start": v(-191.5, 204.25) * mm, "end": v(-191.5, -204.25) * mm});
            skCircle(sketch, "E888", {"center": v(-186.5, -194.25) * mm, "radius": 1.5 * mm});
            skCircle(sketch, "E889", {"center": v(-171.5, -194.25) * mm, "radius": 1.5 * mm});
            skLineSegment(sketch, "E890", {"start": v(-191.5, 217.25) * mm, "end": v(-191.5, 204.25) * mm});
            skLineSegment(sketch, "E891", {"start": v(-191.5, 217.25) * mm, "end": v(-151.5, 217.25) * mm});
            skLineSegment(sketch, "E892", {"start": v(-151.5, 217.25) * mm, "end": v(-151.5, 204.25) * mm});
            skLineSegment(sketch, "E893.bottom", {"start": v(-176.5, 214.25) * mm, "end": v(-166.5, 214.25) * mm});
            skLineSegment(sketch, "E893.top", {"start": v(-176.5, 211.25) * mm, "end": v(-166.5, 211.25) * mm});
            skLineSegment(sketch, "E893.left", {"start": v(-176.5, 214.25) * mm, "end": v(-176.5, 211.25) * mm});
            skLineSegment(sketch, "E893.right", {"start": v(-166.5, 214.25) * mm, "end": v(-166.5, 211.25) * mm});
            skPoint(sketch, "E894.middle", {"position": v(-171.5, 212.75) * mm});
            skPoint(sketch, "E894.middle.positionSnap0", {"position": v(-171.5, 211.25) * mm});
            skPoint(sketch, "E894.middle.positionSnap1", {"position": v(-176.5, 212.75) * mm});
            skPoint(sketch, "E894.centerSnap0", {"position": v(-171.5, 211.25) * mm});
            skPoint(sketch, "E894.centerSnap1", {"position": v(-176.5, 212.75) * mm});
            skCircle(sketch, "E895", {"center": v(-181.5, 212.75) * mm, "radius": 1.5 * mm});
            skLineSegment(sketch, "E896.bottom", {"start": v(526.1, 146.25) * mm, "end": v(526.1, 98.25) * mm});
            skLineSegment(sketch, "E896.right", {"start": v(526.1, 98.25) * mm, "end": v(498.1, 98.25) * mm});
            skLineSegment(sketch, "E897.bottom", {"start": v(498.1, 98.25) * mm, "end": v(498.1, 146.25) * mm});
            skLineSegment(sketch, "E897.right", {"start": v(498.1, 146.25) * mm, "end": v(526.1, 146.25) * mm});
            skCircle(sketch, "E898", {"center": v(492.1, 122.25) * mm, "radius": 1.5 * mm});
            skCircle(sketch, "E899", {"center": v(532.1, 122.25) * mm, "radius": 1.5 * mm});
            skCircle(sketch, "E900", {"center": v(-215.4, -56.75) * mm, "radius": 1.5 * mm});
            skCircle(sketch, "E901", {"center": v(-215.4, -177.75) * mm, "radius": 1.5 * mm});
            skCircle(sketch, "E902", {"center": v(-215.4, 35.25) * mm, "radius": 1.5 * mm});
            skCircle(sketch, "E903", {"center": v(-215.4, 126.25) * mm, "radius": 1.5 * mm});
            skLineSegment(sketch, "E904.bottom", {"start": v(-213.9, 181.25) * mm, "end": v(-216.9, 181.25) * mm});
            skLineSegment(sketch, "E904.top", {"start": v(-213.9, 201.25) * mm, "end": v(-216.9, 201.25) * mm});
            skLineSegment(sketch, "E904.left", {"start": v(-213.9, 181.25) * mm, "end": v(-213.9, 201.25) * mm});
            skLineSegment(sketch, "E904.right", {"start": v(-216.9, 181.25) * mm, "end": v(-216.9, 201.25) * mm});
            skPoint(sketch, "E904.middle", {"position": v(-215.4, 191.25) * mm});
            skLineSegment(sketch, "E905.bottom", {"start": v(-216.9, 105.75) * mm, "end": v(-213.9, 105.75) * mm});
            skLineSegment(sketch, "E905.top", {"start": v(-216.9, 115.75) * mm, "end": v(-213.9, 115.75) * mm});
            skLineSegment(sketch, "E905.left", {"start": v(-216.9, 105.75) * mm, "end": v(-216.9, 115.75) * mm});
            skLineSegment(sketch, "E905.right", {"start": v(-213.9, 105.75) * mm, "end": v(-213.9, 115.75) * mm});
            skPoint(sketch, "E905.middle", {"position": v(-215.4, 110.75) * mm});
            skLineSegment(sketch, "E906.bottom", {"start": v(-216.9, 45.75) * mm, "end": v(-213.9, 45.75) * mm});
            skLineSegment(sketch, "E906.top", {"start": v(-216.9, 55.75) * mm, "end": v(-213.9, 55.75) * mm});
            skLineSegment(sketch, "E906.left", {"start": v(-216.9, 45.75) * mm, "end": v(-216.9, 55.75) * mm});
            skLineSegment(sketch, "E906.right", {"start": v(-213.9, 45.75) * mm, "end": v(-213.9, 55.75) * mm});
            skPoint(sketch, "E906.middle", {"position": v(-215.4, 50.75) * mm});
            skLineSegment(sketch, "E907.bottom", {"start": v(-216.9, -16.25) * mm, "end": v(-213.9, -16.25) * mm});
            skLineSegment(sketch, "E907.top", {"start": v(-216.9, -6.25) * mm, "end": v(-213.9, -6.25) * mm});
            skLineSegment(sketch, "E907.left", {"start": v(-216.9, -16.25) * mm, "end": v(-216.9, -6.25) * mm});
            skLineSegment(sketch, "E907.right", {"start": v(-213.9, -16.25) * mm, "end": v(-213.9, -6.25) * mm});
            skPoint(sketch, "E907.middle", {"position": v(-215.4, -11.25) * mm});
            skLineSegment(sketch, "E908.bottom", {"start": v(-216.9, -78.25) * mm, "end": v(-213.9, -78.25) * mm});
            skLineSegment(sketch, "E908.top", {"start": v(-216.9, -68.25) * mm, "end": v(-213.9, -68.25) * mm});
            skLineSegment(sketch, "E908.left", {"start": v(-216.9, -78.25) * mm, "end": v(-216.9, -68.25) * mm});
            skLineSegment(sketch, "E908.right", {"start": v(-213.9, -78.25) * mm, "end": v(-213.9, -68.25) * mm});
            skPoint(sketch, "E908.middle", {"position": v(-215.4, -73.25) * mm});
            skLineSegment(sketch, "E909.bottom", {"start": v(-216.9, -138.25) * mm, "end": v(-213.9, -138.25) * mm});
            skLineSegment(sketch, "E909.top", {"start": v(-216.9, -128.25) * mm, "end": v(-213.9, -128.25) * mm});
            skLineSegment(sketch, "E909.left", {"start": v(-216.9, -138.25) * mm, "end": v(-216.9, -128.25) * mm});
            skLineSegment(sketch, "E909.right", {"start": v(-213.9, -138.25) * mm, "end": v(-213.9, -128.25) * mm});
            skPoint(sketch, "E909.middle", {"position": v(-215.4, -133.25) * mm});
            skLineSegment(sketch, "E910.bottom", {"start": v(-216.9, -201.25) * mm, "end": v(-213.9, -201.25) * mm});
            skLineSegment(sketch, "E910.top", {"start": v(-216.9, -188.25) * mm, "end": v(-213.9, -188.25) * mm});
            skLineSegment(sketch, "E910.left", {"start": v(-216.9, -201.25) * mm, "end": v(-216.9, -188.25) * mm});
            skLineSegment(sketch, "E910.right", {"start": v(-213.9, -201.25) * mm, "end": v(-213.9, -188.25) * mm});
            skPoint(sketch, "E910.middle", {"position": v(-215.4, -194.75) * mm});
            skLineSegment(sketch, "E911", {"start": v(-262.9, -204.25) * mm, "end": v(-210.9, -204.25) * mm});
            skLineSegment(sketch, "E912", {"start": v(-210.9, -204.25) * mm, "end": v(-210.9, 204.25) * mm});
            skLineSegment(sketch, "E913", {"start": v(-210.9, 204.25) * mm, "end": v(-262.9, 204.25) * mm});
            skLineSegment(sketch, "E914", {"start": v(-262.9, 204.25) * mm, "end": v(-262.9, -204.25) * mm});
            skCircle(sketch, "E915", {"center": v(-252.9, -194.25) * mm, "radius": 1.5 * mm});
            skCircle(sketch, "E916", {"center": v(-222.9, -194.25) * mm, "radius": 1.5 * mm});
            skLineSegment(sketch, "E917", {"start": v(-262.9, 204.25) * mm, "end": v(-262.9, 217.25) * mm});
            skLineSegment(sketch, "E918", {"start": v(-262.9, 217.25) * mm, "end": v(-210.9, 217.25) * mm});
            skLineSegment(sketch, "E919", {"start": v(-210.9, 217.25) * mm, "end": v(-210.9, 204.25) * mm});
            skLineSegment(sketch, "E920.bottom", {"start": v(-249.9, 211.25) * mm, "end": v(-259.9, 211.25) * mm});
            skLineSegment(sketch, "E920.top", {"start": v(-249.9, 214.25) * mm, "end": v(-259.9, 214.25) * mm});
            skLineSegment(sketch, "E920.left", {"start": v(-249.9, 211.25) * mm, "end": v(-249.9, 214.25) * mm});
            skLineSegment(sketch, "E920.right", {"start": v(-259.9, 211.25) * mm, "end": v(-259.9, 214.25) * mm});
            skPoint(sketch, "E920.middle", {"position": v(-254.9, 212.75) * mm});
            skCircle(sketch, "E921", {"center": v(-242.4, 212.75) * mm, "radius": 1.5 * mm});
            skLineSegment(sketch, "E922.bottom", {"start": v(-234.9, 214.25) * mm, "end": v(-224.9, 214.25) * mm});
            skLineSegment(sketch, "E922.top", {"start": v(-234.9, 211.25) * mm, "end": v(-224.9, 211.25) * mm});
            skLineSegment(sketch, "E922.left", {"start": v(-234.9, 214.25) * mm, "end": v(-234.9, 211.25) * mm});
            skLineSegment(sketch, "E922.right", {"start": v(-224.9, 214.25) * mm, "end": v(-224.9, 211.25) * mm});
            skPoint(sketch, "E922.middle", {"position": v(-229.9, 212.75) * mm});
            skSolve(sketch);
        }
        {
            var Q0;
            Q0=makeQuery(id+"F2.imprint","IMPRINT",FACE,{"disambiguationData":[TD([[makeQuery(id+"F2.imprint","IMPRINT",EDGE,{"derivedFrom":sQuery(id+"F2.wireOp",EDGE,"E1")}),-1.0]])]});
            var Q1;
            Q1=makeQuery(id+"F2.imprint","IMPRINT",FACE,{"disambiguationData":[TD([[makeQuery(id+"F2.imprint","IMPRINT",EDGE,{"derivedFrom":sQuery(id+"F2.wireOp",EDGE,"E325")}),-1.0]])]});
            var Q2;
            Q2=makeQuery(id+"F2.imprint","IMPRINT",FACE,{"disambiguationData":[TD([[makeQuery(id+"F2.imprint","IMPRINT",EDGE,{"derivedFrom":sQuery(id+"F2.wireOp",EDGE,"P3LHc5l0-MO9D-QgOO-6sgr-6ZDbjwwaGl83")}),1.0]])]});
            var Q3;
            Q3=makeQuery(id+"F2.imprint","IMPRINT",FACE,{"disambiguationData":[TD([[makeQuery(id+"F2.imprint","IMPRINT",EDGE,{"derivedFrom":sQuery(id+"F2.wireOp",EDGE,"EHVwzmSC-He1n-wpOQ-PZVY-d6QDQvOVziOF")}),1.0]])]});
            var Q4;
            Q4=makeQuery(id+"F2.imprint","IMPRINT",FACE,{"disambiguationData":[TD([[makeQuery(id+"F2.imprint","IMPRINT",EDGE,{"derivedFrom":sQuery(id+"F2.wireOp",EDGE,"5W8SQkOr-2eFS-U1uv-7WF2-2BYrs4aBr38E")}),1.0]])]});
            var Q5;
            Q5=makeQuery(id+"F2.imprint","IMPRINT",FACE,{"disambiguationData":[TD([[makeQuery(id+"F2.imprint","IMPRINT",EDGE,{"derivedFrom":sQuery(id+"F2.wireOp",EDGE,"AksDZKoc-2EWq-vj4X-XMiu-WDsa9oOHHC8E")}),1.0]])]});
            var Q6;
            Q6=makeQuery(id+"F2.imprint","IMPRINT",FACE,{"disambiguationData":[TD([[makeQuery(id+"F2.imprint","IMPRINT",EDGE,{"derivedFrom":sQuery(id+"F2.wireOp",EDGE,"vj80hFJn-AHAh-ara7-uQU3-qOLV3BnwTaf8")}),1.0]])]});
            var Q7;
            Q7=makeQuery(id+"F2.imprint","IMPRINT",FACE,{"disambiguationData":[TD([[makeQuery(id+"F2.imprint","IMPRINT",EDGE,{"derivedFrom":sQuery(id+"F2.wireOp",EDGE,"5W8SQkOr-2eFS-U1uv-7WF2-2BYrs4aBr38E")}),-1.0]])]});
            extrude(context, id + "F3", {"entities" : qUnion([Q0, Q1, Q2, Q3, Q4, Q5, Q6, Q7]), "depth" : 5 * mm, "offsetDistance" : 25 * mm});
        }
        {
            var Q0;
            Q0=makeQuery(id+"F2.imprint","IMPRINT",FACE,{"disambiguationData":[TD([[makeQuery(id+"F2.imprint","IMPRINT",EDGE,{"derivedFrom":sQuery(id+"F2.wireOp",EDGE,"E321")}),-1.0]])]});
            var Q1;
            Q1=makeQuery(id+"F2.imprint","IMPRINT",FACE,{"disambiguationData":[TD([[makeQuery(id+"F2.imprint","IMPRINT",EDGE,{"derivedFrom":sQuery(id+"F2.wireOp",EDGE,"E322")}),-1.0]])]});
            extrude(context, id + "F4", {"entities" : qUnion([Q0, Q1]), "operationType" : NewBodyOperationType.ADD, "depth" : 2 * mm, "offsetDistance" : 25 * mm});
        }
        {
            var Q0;
            Q0=makeQuery(id+"F2.imprint","IMPRINT",FACE,{"disambiguationData":[TD([[makeQuery(id+"F2.imprint","IMPRINT",EDGE,{"derivedFrom":sQuery(id+"F2.wireOp",EDGE,"E339")}),-1.0]])]});
            var Q1;
            Q1=makeQuery(id+"F2.imprint","IMPRINT",FACE,{"disambiguationData":[TD([[makeQuery(id+"F2.imprint","IMPRINT",EDGE,{"derivedFrom":sQuery(id+"F2.wireOp",EDGE,"E648")}),1.0]])]});
            var Q2;
            Q2=makeQuery(id+"F2.imprint","IMPRINT",FACE,{"disambiguationData":[TD([[makeQuery(id+"F2.imprint","IMPRINT",EDGE,{"derivedFrom":sQuery(id+"F2.wireOp",EDGE,"E647")}),1.0]])]});
            var Q3;
            Q3=makeQuery(id+"F2.imprint","IMPRINT",FACE,{"disambiguationData":[TD([[makeQuery(id+"F2.imprint","IMPRINT",EDGE,{"derivedFrom":sQuery(id+"F2.wireOp",EDGE,"E649")}),1.0]])]});
            extrude(context, id + "F5", {"entities" : qUnion([Q0, Q1, Q2, Q3]), "depth" : 3 * mm, "offsetDistance" : 25 * mm});
        }
        {
            var Q0;
            Q0=makeQuery(id+"F2.imprint","IMPRINT",FACE,{"disambiguationData":[TD([[makeQuery(id+"F2.imprint","IMPRINT",EDGE,{"derivedFrom":sQuery(id+"F2.wireOp",EDGE,"E650.bottom")}),-1.0]])]});
            extrude(context, id + "F6", {"entities" : qUnion([Q0]), "depth" : 50 * mm, "offsetDistance" : 25 * mm});
        }
        {
            var Q0;
            Q0=makeQuery(id+"F2.imprint","IMPRINT",FACE,{"disambiguationData":[TD([[makeQuery(id+"F2.imprint","IMPRINT",EDGE,{"derivedFrom":sQuery(id+"F2.wireOp",EDGE,"E651")}),1.0]])]});
            extrude(context, id + "F7", {"entities" : qUnion([Q0]), "depth" : 60 * mm, "offsetDistance" : 25 * mm});
        }
        {
            var Q0;
            Q0=makeQuery(id+"F2.imprint","IMPRINT",FACE,{"disambiguationData":[TD([[makeQuery(id+"F2.imprint","IMPRINT",EDGE,{"derivedFrom":sQuery(id+"F2.wireOp",EDGE,"E652.bottom")}),-1.0]])]});
            extrude(context, id + "F8", {"entities" : qUnion([Q0]), "depth" : 25 * mm, "offsetDistance" : 25 * mm});
        }
        {
            var Q0;
            Q0=makeQuery(id+"F2.imprint","IMPRINT",FACE,{"disambiguationData":[TD([[makeQuery(id+"F2.imprint","IMPRINT",EDGE,{"derivedFrom":sQuery(id+"F2.wireOp",EDGE,"E653.bottom")}),-1.0]])]});
            extrude(context, id + "F9", {"entities" : qUnion([Q0]), "depth" : 57 * mm, "offsetDistance" : 25 * mm});
        }
        {
            var Q0;
            Q0=makeQuery(id+"F2.imprint","IMPRINT",FACE,{"disambiguationData":[TD([[makeQuery(id+"F2.imprint","IMPRINT",EDGE,{"derivedFrom":sQuery(id+"F2.wireOp",EDGE,"E655.bottom")}),1.0]])]});
            extrude(context, id + "F10", {"entities" : qUnion([Q0]), "depth" : 26 * mm, "offsetDistance" : 25 * mm});
        }
        {
            var Q0;
            Q0=makeQuery(id+"F2.imprint","IMPRINT",FACE,{"disambiguationData":[TD([[makeQuery(id+"F2.imprint","IMPRINT",EDGE,{"derivedFrom":sQuery(id+"F2.wireOp",EDGE,"E672")}),-1.0]])]});
            var Q1;
            Q1=makeQuery(id+"F2.imprint","IMPRINT",FACE,{"disambiguationData":[TD([[makeQuery(id+"F2.imprint","IMPRINT",EDGE,{"derivedFrom":sQuery(id+"F2.wireOp",EDGE,"E683")}),-1.0]])]});
            var Q2;
            Q2=makeQuery(id+"F2.imprint","IMPRINT",FACE,{"disambiguationData":[TD([[makeQuery(id+"F2.imprint","IMPRINT",EDGE,{"derivedFrom":sQuery(id+"F2.wireOp",EDGE,"E694")}),-1.0]])]});
            var Q3;
            Q3=makeQuery(id+"F2.imprint","IMPRINT",FACE,{"disambiguationData":[TD([[makeQuery(id+"F2.imprint","IMPRINT",EDGE,{"derivedFrom":sQuery(id+"F2.wireOp",EDGE,"E705")}),-1.0]])]});
            var Q4;
            Q4=makeQuery(id+"F2.imprint","IMPRINT",FACE,{"disambiguationData":[TD([[makeQuery(id+"F2.imprint","IMPRINT",EDGE,{"derivedFrom":sQuery(id+"F2.wireOp",EDGE,"E726")}),-1.0]])]});
            var Q5;
            Q5=makeQuery(id+"F2.imprint","IMPRINT",FACE,{"disambiguationData":[TD([[makeQuery(id+"F2.imprint","IMPRINT",EDGE,{"derivedFrom":sQuery(id+"F2.wireOp",EDGE,"E730")}),-1.0]])]});
            var Q6;
            Q6=makeQuery(id+"F2.imprint","IMPRINT",FACE,{"disambiguationData":[TD([[makeQuery(id+"F2.imprint","IMPRINT",EDGE,{"derivedFrom":sQuery(id+"F2.wireOp",EDGE,"E756")}),-1.0]])]});
            var Q7;
            {var subQ4=sQuery(id+"F2.wireOp",EDGE,"E787.bottom");Q7=makeQuery(id+"F2.imprint","IMPRINT",FACE,{"disambiguationData":[TD([[makeQuery(id+"F2.imprint","IMPRINT",EDGE,{"derivedFrom":subQ4}),-1.0]])]});}
            var Q8;
            {var subQ2=sQuery(id+"F2.wireOp",EDGE,"E787.top");Q8=makeQuery(id+"F2.imprint","IMPRINT",FACE,{"disambiguationData":[TD([[makeQuery(id+"F2.imprint","IMPRINT",EDGE,{"derivedFrom":subQ2}),1.0]])]});}
            var Q9;
            Q9=makeQuery(id+"F2.imprint","IMPRINT",FACE,{"disambiguationData":[TD([[makeQuery(id+"F2.imprint","IMPRINT",EDGE,{"derivedFrom":sQuery(id+"F2.wireOp",EDGE,"E815.bottom")}),1.0]])]});
            var Q10;
            Q10=makeQuery(id+"F2.imprint","IMPRINT",FACE,{"disambiguationData":[TD([[makeQuery(id+"F2.imprint","IMPRINT",EDGE,{"derivedFrom":sQuery(id+"F2.wireOp",EDGE,"E814.bottom")}),-1.0]])]});
            var Q11;
            {var subQ1=sQuery(id+"F2.wireOp",EDGE,"E790.bottom");Q11=makeQuery(id+"F2.imprint","IMPRINT",FACE,{"disambiguationData":[TD([[makeQuery(id+"F2.imprint","IMPRINT",EDGE,{"derivedFrom":subQ1}),-1.0]])]});}
            var Q12;
            {var subQ1=sQuery(id+"F2.wireOp",EDGE,"E790.top");Q12=makeQuery(id+"F2.imprint","IMPRINT",FACE,{"disambiguationData":[TD([[makeQuery(id+"F2.imprint","IMPRINT",EDGE,{"derivedFrom":subQ1}),1.0]])]});}
            var Q13;
            Q13=makeQuery(id+"F2.imprint","IMPRINT",FACE,{"disambiguationData":[TD([[makeQuery(id+"F2.imprint","IMPRINT",EDGE,{"derivedFrom":sQuery(id+"F2.wireOp",EDGE,"E767")}),-1.0]])]});
            var Q14;
            {var subQ7=sQuery(id+"F2.wireOp",EDGE,"E786.top");Q14=makeQuery(id+"F2.imprint","IMPRINT",FACE,{"disambiguationData":[TD([[makeQuery(id+"F2.imprint","IMPRINT",EDGE,{"derivedFrom":subQ7}),-1.0]])]});}
            var Q15;
            Q15=makeQuery(id+"F2.imprint","IMPRINT",FACE,{"disambiguationData":[TD([[makeQuery(id+"F2.imprint","IMPRINT",EDGE,{"derivedFrom":sQuery(id+"F2.wireOp",EDGE,"E828.bottom")}),1.0]])]});
            var Q16;
            Q16=makeQuery(id+"F2.imprint","IMPRINT",FACE,{"disambiguationData":[TD([[makeQuery(id+"F2.imprint","IMPRINT",EDGE,{"derivedFrom":sQuery(id+"F2.wireOp",EDGE,"E816.bottom")}),1.0]])]});
            var Q17;
            {var subQ4=sQuery(id+"F2.wireOp",EDGE,"E786.bottom");Q17=makeQuery(id+"F2.imprint","IMPRINT",FACE,{"disambiguationData":[TD([[makeQuery(id+"F2.imprint","IMPRINT",EDGE,{"derivedFrom":subQ4}),1.0]])]});}
            var Q18;
            Q18=makeQuery(id+"F2.imprint","IMPRINT",FACE,{"disambiguationData":[TD([[makeQuery(id+"F2.imprint","IMPRINT",EDGE,{"derivedFrom":sQuery(id+"F2.wireOp",EDGE,"E830.bottom")}),-1.0]])]});
            var Q19;
            Q19=makeQuery(id+"F2.imprint","IMPRINT",FACE,{"disambiguationData":[TD([[makeQuery(id+"F2.imprint","IMPRINT",EDGE,{"derivedFrom":sQuery(id+"F2.wireOp",EDGE,"E829.bottom")}),-1.0]])]});
            var Q20;
            {var subQ1=sQuery(id+"F2.wireOp",EDGE,"E789.bottom");Q20=makeQuery(id+"F2.imprint","IMPRINT",FACE,{"disambiguationData":[TD([[makeQuery(id+"F2.imprint","IMPRINT",EDGE,{"derivedFrom":subQ1}),1.0]])]});}
            var Q21;
            {var subQ0=sQuery(id+"F2.wireOp",EDGE,"E791");Q21=makeQuery(id+"F2.imprint","IMPRINT",FACE,{"disambiguationData":[TD([[makeQuery(id+"F2.imprint","IMPRINT",EDGE,{"derivedFrom":subQ0}),-1.0]])]});}
            var Q22;
            Q22=makeQuery(id+"F2.imprint","IMPRINT",FACE,{"disambiguationData":[TD([[makeQuery(id+"F2.imprint","IMPRINT",EDGE,{"derivedFrom":sQuery(id+"F2.wireOp",EDGE,"E873")}),-1.0]])]});
            var Q23;
            Q23=makeQuery(id+"F2.imprint","IMPRINT",FACE,{"disambiguationData":[TD([[makeQuery(id+"F2.imprint","IMPRINT",EDGE,{"derivedFrom":sQuery(id+"F2.wireOp",EDGE,"E886")}),-1.0]])]});
            var Q24;
            Q24=makeQuery(id+"F2.imprint","IMPRINT",FACE,{"disambiguationData":[TD([[makeQuery(id+"F2.imprint","IMPRINT",EDGE,{"derivedFrom":sQuery(id+"F2.wireOp",EDGE,"E900")}),-1.0]])]});
            var Q25;
            Q25=makeQuery(id+"F2.imprint","IMPRINT",FACE,{"disambiguationData":[TD([[makeQuery(id+"F2.imprint","IMPRINT",EDGE,{"derivedFrom":sQuery(id+"F2.wireOp",EDGE,"E913")}),-1.0]])]});
            extrude(context, id + "F11", {"entities" : qUnion([Q0, Q1, Q2, Q3, Q4, Q5, Q6, Q7, Q8, Q9, Q10, Q11, Q12, Q13, Q14, Q15, Q16, Q17, Q18, Q19, Q20, Q21, Q22, Q23, Q24, Q25]), "depth" : 3 * mm, "offsetDistance" : 25 * mm});
        }
        {
            var Q0;
            Q0=makeQuery(id+"F2.imprint","IMPRINT",FACE,{"disambiguationData":[TD([[makeQuery(id+"F2.imprint","IMPRINT",EDGE,{"derivedFrom":sQuery(id+"F2.wireOp",EDGE,"E842")}),-1.0]])]});
            var Q1;
            {var subQ0=sQuery(id+"F2.wireOp",EDGE,"E849");Q1=makeQuery(id+"F2.imprint","IMPRINT",FACE,{"disambiguationData":[TD([[makeQuery(id+"F2.imprint","IMPRINT",EDGE,{"derivedFrom":subQ0}),1.0]])]});}
            extrude(context, id + "F12", {"entities" : qUnion([Q0, Q1]), "depth" : 6 * mm, "offsetDistance" : 25 * mm});
        }
    });
